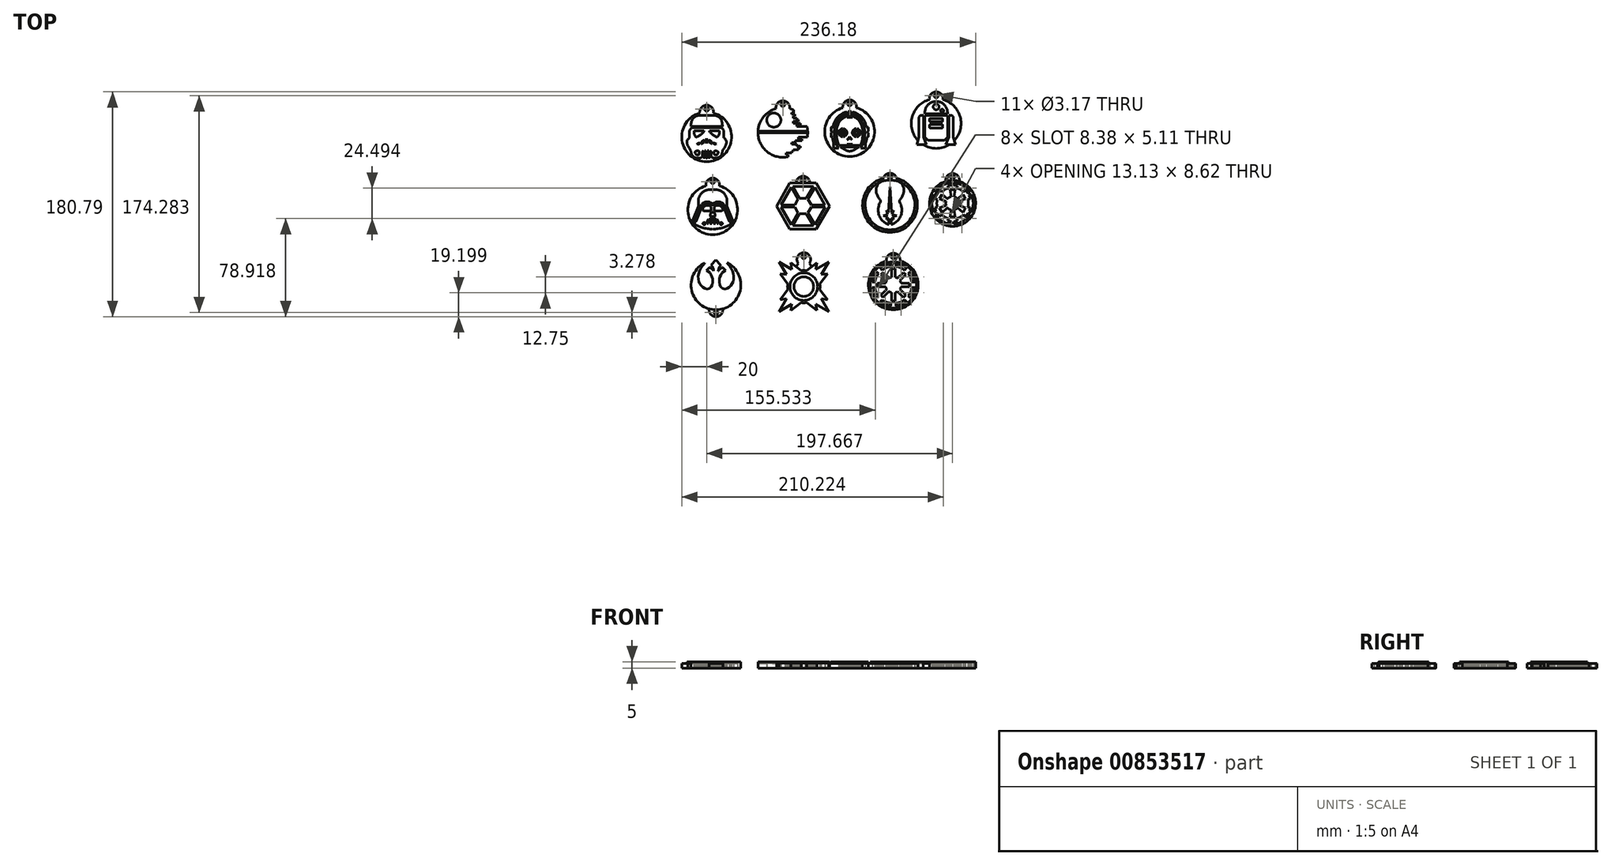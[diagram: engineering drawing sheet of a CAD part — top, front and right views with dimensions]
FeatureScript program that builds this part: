
annotation { "Feature Type Name" : "Feature", "Feature Type Description" : "" }
export const myFeature = defineFeature(function(context is Context, id is Id, definition is map)
    precondition{}
    {
        {
            var Q0;
            Q0=qCreatedBy(makeId("Top.planeOp"),FACE);
            var sketch = newSketch(context, id + "F0", { "sketchPlane" : qUnion([Q0])});
            skCircle(sketch, "E0", {"center": v(-100.44, 60.78) * mm, "radius": 20 * mm});
            skArc(sketch, "E1", {"start": v(-95, 80.02) * mm, "mid": v(-100.44, 86.28) * mm, "end": v(-105.89, 80.02) * mm});
            skCircle(sketch, "E2", {"center": v(-100.44, 83.03) * mm, "radius": 1.59 * mm});
            skLineSegment(sketch, "E3", {"start": v(-100.44, 78.18) * mm, "end": v(-105.77, 78.18) * mm});
            skFitSpline(sketch, "E4", {"points": [v(-105.77, 78.18) * mm, v(-108.26, 77.7) * mm, v(-111.1, 76.07) * mm, v(-112.23, 74.28) * mm, v(-112.98, 71.44) * mm, v(-113.03, 69.29) * mm], "startDerivative": vector(-12.14, -1.3) * mm, "endDerivative": vector(0.48, -11.2) * mm});
            skLineSegment(sketch, "E5", {"start": v(-113.03, 69.29) * mm, "end": v(-100.44, 69.29) * mm});
            skLineSegment(sketch, "E6", {"start": v(-100.44, 68.37) * mm, "end": v(-112.52, 68.37) * mm});
            skLineSegment(sketch, "E7", {"start": v(-112.52, 68.37) * mm, "end": v(-114.2, 66.04) * mm});
            skLineSegment(sketch, "E8", {"start": v(-114.2, 66.04) * mm, "end": v(-114.2, 60.06) * mm});
            skFitSpline(sketch, "E9", {"points": [v(-114.2, 60.06) * mm, v(-115.3, 59.1) * mm, v(-116.22, 57.54) * mm, v(-116.26, 55.78) * mm, v(-115.42, 53.27) * mm, v(-113.28, 49.95) * mm], "startDerivative": vector(-7.03, -5.26) * mm, "endDerivative": vector(9.04, -12.66) * mm});
            skFitSpline(sketch, "E10", {"points": [v(-113.28, 49.95) * mm, v(-113.02, 48.5) * mm, v(-112.3, 46.4) * mm, v(-111.03, 44.84) * mm, v(-109.24, 44) * mm, v(-107.26, 43.62) * mm, v(-105.24, 44.07) * mm, v(-103.86, 44.76) * mm], "startDerivative": vector(1.7, -10.88) * mm, "endDerivative": vector(9.96, 5.56) * mm});
            skLineSegment(sketch, "E11", {"start": v(-103.86, 44.76) * mm, "end": v(-103.86, 49.13) * mm});
            skLineSegment(sketch, "E12", {"start": v(-103.86, 49.13) * mm, "end": v(-103.07, 49.69) * mm});
            skLineSegment(sketch, "E13", {"start": v(-103.07, 49.69) * mm, "end": v(-103.07, 44.4) * mm});
            skFitSpline(sketch, "E14", {"points": [v(-103.07, 44.4) * mm, v(-102.64, 43.98) * mm, v(-102.12, 44.11) * mm, v(-101.98, 44.4) * mm], "startDerivative": vector(1, -1.45) * mm, "endDerivative": vector(0.3, 1.11) * mm});
            skLineSegment(sketch, "E15", {"start": v(-101.98, 44.4) * mm, "end": v(-101.98, 49.69) * mm});
            skLineSegment(sketch, "E16", {"start": v(-101.98, 49.69) * mm, "end": v(-101.2, 49.69) * mm});
            skLineSegment(sketch, "E17", {"start": v(-101.2, 49.69) * mm, "end": v(-101.2, 44.4) * mm});
            skFitSpline(sketch, "E18", {"points": [v(-101.2, 44.4) * mm, v(-100.97, 43.94) * mm, v(-100.61, 43.77) * mm, v(-100.44, 43.77) * mm], "startDerivative": vector(0.44, -1.3) * mm, "endDerivative": vector(0.66, 0.06) * mm});
            skLineSegment(sketch, "E19", {"start": v(-102.6, 65.55) * mm, "end": v(-110.61, 65.55) * mm});
            skLineSegment(sketch, "E20", {"start": v(-102.6, 65.55) * mm, "end": v(-102.6, 64.96) * mm});
            skFitSpline(sketch, "E21", {"points": [v(-110.61, 65.55) * mm, v(-110.61, 63.59) * mm, v(-110, 61.89) * mm, v(-108.94, 60.78) * mm, v(-107.62, 61) * mm, v(-105.2, 62.61) * mm, v(-102.6, 64.96) * mm], "startDerivative": vector(-0.88, -12.5) * mm, "endDerivative": vector(11.82, 11.31) * mm});
            skFitSpline(sketch, "E22", {"points": [v(-108.1, 55.17) * mm, v(-107.08, 55.66) * mm, v(-106, 55.74) * mm, v(-105.95, 55.5) * mm, v(-106.43, 55.06) * mm, v(-107.16, 54.9) * mm, v(-108.1, 55.17) * mm]});
            skLineSegment(sketch, "E23.bottom", {"start": v(-100.44, 58.8) * mm, "end": v(-99.36, 58.8) * mm});
            skLineSegment(sketch, "E23.top", {"start": v(-100.44, 56.6) * mm, "end": v(-99.36, 56.6) * mm});
            skLineSegment(sketch, "E23.left", {"start": v(-100.44, 58.8) * mm, "end": v(-100.44, 56.6) * mm});
            skLineSegment(sketch, "E23.right", {"start": v(-99.36, 58.8) * mm, "end": v(-99.36, 56.6) * mm});
            skLineSegment(sketch, "E24", {"start": v(-98.39, 58.2) * mm, "end": v(-98.39, 56.48) * mm});
            skLineSegment(sketch, "E25", {"start": v(-98.39, 56.48) * mm, "end": v(-96.69, 55.32) * mm});
            skLineSegment(sketch, "E26", {"start": v(-96.69, 55.32) * mm, "end": v(-96.1, 55.32) * mm});
            skLineSegment(sketch, "E27", {"start": v(-96.1, 55.32) * mm, "end": v(-96.1, 56.03) * mm});
            skFitSpline(sketch, "E28", {"points": [v(-98.39, 58.2) * mm, v(-97.3, 57.74) * mm, v(-96.51, 57) * mm, v(-96.1, 56.03) * mm], "startDerivative": vector(3.26, -1.14) * mm, "endDerivative": vector(0.98, -3.12) * mm});
            skFitSpline(sketch, "E29", {"points": [v(-108.72, 49.43) * mm, v(-109.59, 48.85) * mm, v(-109.81, 47.92) * mm, v(-109.01, 46.77) * mm, v(-107.66, 46.12) * mm, v(-106.64, 46.5) * mm, v(-106.32, 47.21) * mm, v(-106.29, 48.4) * mm, v(-106.54, 49.14) * mm, v(-107.34, 49.65) * mm, v(-108.72, 49.43) * mm]});
            skLineSegment(sketch, "E30.MirrorCS", {"start": v(-100.44, 78.18) * mm, "end": v(-95.11, 78.18) * mm});
            skFitSpline(sketch, "E31.MirrorCS", {"points": [v(-95.11, 78.18) * mm, v(-92.62, 77.7) * mm, v(-89.78, 76.07) * mm, v(-88.65, 74.28) * mm, v(-87.9, 71.44) * mm, v(-87.85, 69.29) * mm], "startDerivative": vector(12.14, -1.3) * mm, "endDerivative": vector(-0.48, -11.2) * mm});
            skLineSegment(sketch, "E32.MirrorCS", {"start": v(-87.85, 69.29) * mm, "end": v(-100.44, 69.29) * mm});
            skLineSegment(sketch, "E33.MirrorCS", {"start": v(-100.44, 68.37) * mm, "end": v(-88.36, 68.37) * mm});
            skLineSegment(sketch, "E34.MirrorCS", {"start": v(-88.36, 68.37) * mm, "end": v(-86.68, 66.04) * mm});
            skLineSegment(sketch, "E35.MirrorCS", {"start": v(-86.68, 66.04) * mm, "end": v(-86.68, 60.06) * mm});
            skLineSegment(sketch, "E36.MirrorCS", {"start": v(-98.28, 65.55) * mm, "end": v(-90.27, 65.55) * mm});
            skFitSpline(sketch, "E37.MirrorCS", {"points": [v(-90.27, 65.55) * mm, v(-90.27, 63.59) * mm, v(-90.89, 61.89) * mm, v(-91.94, 60.78) * mm, v(-93.26, 61) * mm, v(-95.69, 62.61) * mm, v(-98.28, 64.96) * mm], "startDerivative": vector(0.88, -12.5) * mm, "endDerivative": vector(-11.82, 11.31) * mm});
            skLineSegment(sketch, "E38.MirrorCS", {"start": v(-101.52, 58.8) * mm, "end": v(-101.52, 56.6) * mm});
            skLineSegment(sketch, "E39.MirrorCS", {"start": v(-100.44, 58.8) * mm, "end": v(-101.52, 58.8) * mm});
            skLineSegment(sketch, "E40.MirrorCS", {"start": v(-100.44, 56.6) * mm, "end": v(-101.52, 56.6) * mm});
            skFitSpline(sketch, "E41.MirrorC", {"points": [v(-92.78, 55.17) * mm, v(-93.8, 55.66) * mm, v(-94.88, 55.74) * mm, v(-94.93, 55.5) * mm, v(-94.45, 55.06) * mm, v(-93.72, 54.9) * mm, v(-92.78, 55.17) * mm]});
            skLineSegment(sketch, "E42.MirrorCS", {"start": v(-102.5, 56.48) * mm, "end": v(-104.2, 55.32) * mm});
            skLineSegment(sketch, "E43.MirrorCS", {"start": v(-102.5, 58.2) * mm, "end": v(-102.5, 56.48) * mm});
            skLineSegment(sketch, "E44.MirrorCS", {"start": v(-104.2, 55.32) * mm, "end": v(-104.77, 55.32) * mm});
            skLineSegment(sketch, "E45.MirrorCS", {"start": v(-104.77, 55.32) * mm, "end": v(-104.77, 56.03) * mm});
            skFitSpline(sketch, "E46.MirrorCS", {"points": [v(-102.5, 58.2) * mm, v(-103.57, 57.74) * mm, v(-104.37, 57) * mm, v(-104.77, 56.03) * mm], "startDerivative": vector(-3.26, -1.14) * mm, "endDerivative": vector(-0.98, -3.12) * mm});
            skFitSpline(sketch, "E47.MirrorCS", {"points": [v(-86.68, 60.06) * mm, v(-85.57, 59.1) * mm, v(-84.66, 57.54) * mm, v(-84.62, 55.78) * mm, v(-85.46, 53.27) * mm, v(-87.6, 49.95) * mm], "startDerivative": vector(7.03, -5.26) * mm, "endDerivative": vector(-9.04, -12.66) * mm});
            skFitSpline(sketch, "E48.MirrorCS", {"points": [v(-87.6, 49.95) * mm, v(-87.86, 48.5) * mm, v(-88.59, 46.4) * mm, v(-89.85, 44.84) * mm, v(-91.64, 44) * mm, v(-93.62, 43.62) * mm, v(-95.64, 44.07) * mm, v(-97.02, 44.76) * mm], "startDerivative": vector(-1.7, -10.88) * mm, "endDerivative": vector(-9.96, 5.56) * mm});
            skFitSpline(sketch, "E49.MirrorC", {"points": [v(-92.16, 49.43) * mm, v(-91.3, 48.85) * mm, v(-91.07, 47.92) * mm, v(-91.87, 46.77) * mm, v(-93.22, 46.12) * mm, v(-94.24, 46.5) * mm, v(-94.56, 47.21) * mm, v(-94.6, 48.4) * mm, v(-94.34, 49.14) * mm, v(-93.54, 49.65) * mm, v(-92.16, 49.43) * mm]});
            skLineSegment(sketch, "E50.MirrorCS", {"start": v(-97.02, 44.76) * mm, "end": v(-97.02, 49.13) * mm});
            skLineSegment(sketch, "E51.MirrorCS", {"start": v(-97.02, 49.13) * mm, "end": v(-97.8, 49.69) * mm});
            skLineSegment(sketch, "E52.MirrorCS", {"start": v(-97.8, 49.69) * mm, "end": v(-97.8, 44.4) * mm});
            skLineSegment(sketch, "E53.MirrorCS", {"start": v(-98.9, 44.4) * mm, "end": v(-98.9, 49.69) * mm});
            skLineSegment(sketch, "E54.MirrorCS", {"start": v(-98.9, 49.69) * mm, "end": v(-99.67, 49.69) * mm});
            skLineSegment(sketch, "E55.MirrorCS", {"start": v(-99.67, 49.69) * mm, "end": v(-99.67, 44.4) * mm});
            skFitSpline(sketch, "E56.MirrorCS", {"points": [v(-99.67, 44.4) * mm, v(-99.91, 43.94) * mm, v(-100.27, 43.77) * mm, v(-100.44, 43.77) * mm], "startDerivative": vector(-0.44, -1.3) * mm, "endDerivative": vector(-0.66, 0.06) * mm});
            skFitSpline(sketch, "E57.MirrorCS", {"points": [v(-97.8, 44.4) * mm, v(-98.24, 43.98) * mm, v(-98.76, 44.11) * mm, v(-98.9, 44.4) * mm], "startDerivative": vector(-1, -1.45) * mm, "endDerivative": vector(-0.3, 1.11) * mm});
            skLineSegment(sketch, "E58", {"start": v(-98.28, 65.55) * mm, "end": v(-98.28, 64.96) * mm});
            skSolve(sketch);
        }
        {
            var Q0;
            Q0=qCreatedBy(makeId("Top.planeOp"),FACE);
            var sketch = newSketch(context, id + "F1", { "sketchPlane" : qUnion([Q0])});
            skArc(sketch, "E59", {"start": v(-30.66, 82.44) * mm, "mid": v(-59.08, 66.65) * mm, "end": v(-35.01, 44.8) * mm});
            skArc(sketch, "E60", {"start": v(-33.76, 83.6) * mm, "mid": v(-39.21, 89.85) * mm, "end": v(-44.66, 83.6) * mm});
            skCircle(sketch, "E61", {"center": v(-39.21, 86.8) * mm, "radius": 1.59 * mm});
            skCircle(sketch, "E62", {"center": v(-46.46, 74.27) * mm, "radius": 5.66 * mm});
            skLineSegment(sketch, "E63", {"start": v(-30.66, 82.44) * mm, "end": v(-30.66, 80.15) * mm});
            skLineSegment(sketch, "E64", {"start": v(-30.66, 80.15) * mm, "end": v(-32.2, 80.15) * mm});
            skLineSegment(sketch, "E65", {"start": v(-32.2, 80.15) * mm, "end": v(-32.2, 78.86) * mm});
            skLineSegment(sketch, "E66", {"start": v(-32.2, 78.86) * mm, "end": v(-29.52, 78.86) * mm});
            skLineSegment(sketch, "E67", {"start": v(-29.52, 78.86) * mm, "end": v(-29.52, 77.4) * mm});
            skLineSegment(sketch, "E68", {"start": v(-29.52, 77.4) * mm, "end": v(-30.9, 77.4) * mm});
            skLineSegment(sketch, "E69", {"start": v(-30.9, 77.4) * mm, "end": v(-30.9, 75.98) * mm});
            skLineSegment(sketch, "E70", {"start": v(-30.9, 75.98) * mm, "end": v(-28.1, 75.98) * mm});
            skLineSegment(sketch, "E71", {"start": v(-28.1, 75.98) * mm, "end": v(-28.1, 74.48) * mm});
            skLineSegment(sketch, "E72", {"start": v(-28.1, 74.48) * mm, "end": v(-26.61, 74.48) * mm});
            skLineSegment(sketch, "E73", {"start": v(-26.61, 74.48) * mm, "end": v(-26.61, 73.15) * mm});
            skLineSegment(sketch, "E74", {"start": v(-26.61, 73.15) * mm, "end": v(-30.79, 73.15) * mm});
            skLineSegment(sketch, "E75", {"start": v(-30.79, 73.15) * mm, "end": v(-30.79, 71.78) * mm});
            skLineSegment(sketch, "E76", {"start": v(-30.79, 71.78) * mm, "end": v(-25.24, 71.78) * mm});
            skLineSegment(sketch, "E77", {"start": v(-25.24, 71.78) * mm, "end": v(-25.24, 70.29) * mm});
            skLineSegment(sketch, "E78", {"start": v(-25.24, 70.29) * mm, "end": v(-28, 70.29) * mm});
            skLineSegment(sketch, "E79", {"start": v(-28, 70.29) * mm, "end": v(-28, 69.08) * mm});
            skLineSegment(sketch, "E80", {"start": v(-28, 69.08) * mm, "end": v(-19.78, 69.08) * mm});
            skLineSegment(sketch, "E81", {"start": v(-59.18, 65.46) * mm, "end": v(-19.24, 65.46) * mm});
            skLineSegment(sketch, "E82", {"start": v(-59.2, 64.02) * mm, "end": v(-19.21, 64.02) * mm});
            skLineSegment(sketch, "E83", {"start": v(-19.59, 60.49) * mm, "end": v(-26.58, 60.49) * mm});
            skLineSegment(sketch, "E84", {"start": v(-26.58, 60.49) * mm, "end": v(-26.58, 59.12) * mm});
            skLineSegment(sketch, "E85", {"start": v(-26.58, 59.12) * mm, "end": v(-23.87, 59.12) * mm});
            skLineSegment(sketch, "E86", {"start": v(-23.87, 59.12) * mm, "end": v(-23.87, 57.67) * mm});
            skLineSegment(sketch, "E87", {"start": v(-23.87, 57.67) * mm, "end": v(-29.3, 57.67) * mm});
            skLineSegment(sketch, "E88", {"start": v(-29.3, 57.67) * mm, "end": v(-29.3, 56.14) * mm});
            skLineSegment(sketch, "E89", {"start": v(-29.3, 56.14) * mm, "end": v(-32.23, 56.14) * mm});
            skLineSegment(sketch, "E90", {"start": v(-32.23, 56.14) * mm, "end": v(-32.23, 54.92) * mm});
            skLineSegment(sketch, "E91", {"start": v(-32.23, 54.92) * mm, "end": v(-28.03, 54.92) * mm});
            skLineSegment(sketch, "E92", {"start": v(-28.03, 54.92) * mm, "end": v(-28.03, 53.4) * mm});
            skLineSegment(sketch, "E93", {"start": v(-28.03, 53.4) * mm, "end": v(-25.29, 53.4) * mm});
            skLineSegment(sketch, "E94", {"start": v(-25.29, 53.4) * mm, "end": v(-25.29, 51.9) * mm});
            skLineSegment(sketch, "E95", {"start": v(-25.29, 51.9) * mm, "end": v(-26.58, 51.9) * mm});
            skLineSegment(sketch, "E96", {"start": v(-26.58, 51.9) * mm, "end": v(-26.58, 50.46) * mm});
            skLineSegment(sketch, "E97", {"start": v(-26.58, 50.46) * mm, "end": v(-30.82, 50.46) * mm});
            skLineSegment(sketch, "E98", {"start": v(-30.82, 50.46) * mm, "end": v(-30.82, 49.28) * mm});
            skLineSegment(sketch, "E99", {"start": v(-30.82, 49.28) * mm, "end": v(-32.23, 49.28) * mm});
            skLineSegment(sketch, "E100", {"start": v(-32.23, 49.28) * mm, "end": v(-32.23, 47.79) * mm});
            skLineSegment(sketch, "E101", {"start": v(-32.23, 47.79) * mm, "end": v(-36.5, 47.79) * mm});
            skLineSegment(sketch, "E102", {"start": v(-36.5, 47.79) * mm, "end": v(-36.5, 46.45) * mm});
            skLineSegment(sketch, "E103", {"start": v(-36.5, 46.45) * mm, "end": v(-35.01, 46.45) * mm});
            skLineSegment(sketch, "E104", {"start": v(-35.01, 46.45) * mm, "end": v(-35.01, 44.8) * mm});
            skArc(sketch, "E105.trimOffspring", {"start": v(-19.59, 60.49) * mm, "mid": v(-19.22, 64.8) * mm, "end": v(-19.78, 69.08) * mm});
            skSolve(sketch);
        }
        {
            var Q0;
            Q0=qCreatedBy(makeId("Top.planeOp"),FACE);
            var sketch = newSketch(context, id + "F2", { "sketchPlane" : qUnion([Q0])});
            skCircle(sketch, "E106", {"center": v(14.5, 65.01) * mm, "radius": 20 * mm});
            skArc(sketch, "E107", {"start": v(19.94, 84.25) * mm, "mid": v(14.5, 90.51) * mm, "end": v(9.05, 84.25) * mm});
            skCircle(sketch, "E108", {"center": v(14.5, 87.35) * mm, "radius": 1.59 * mm});
            skLineSegment(sketch, "E109.bottom", {"start": v(14.5, 81.26) * mm, "end": v(13.26, 81.26) * mm});
            skLineSegment(sketch, "E109.top", {"start": v(14.5, 77.67) * mm, "end": v(13.26, 77.67) * mm});
            skLineSegment(sketch, "E109.right", {"start": v(13.26, 81.26) * mm, "end": v(13.26, 77.67) * mm});
            skPoint(sketch, "E110.1.internal.snap0", {"position": v(13.26, 79.46) * mm});
            skFitSpline(sketch, "E110", {"points": [v(12.26, 80.95) * mm, v(8.57, 79.46) * mm, v(4.65, 76.5) * mm, v(2.7, 73.58) * mm, v(1.48, 70.56) * mm, v(1.13, 68.67) * mm], "startDerivative": vector(-16.9, -5.64) * mm, "endDerivative": vector(-1.55, -11.93) * mm});
            skLineSegment(sketch, "E111", {"start": v(12.26, 80.95) * mm, "end": v(12.26, 79.13) * mm});
            skFitSpline(sketch, "E112", {"points": [v(12.26, 79.13) * mm, v(9.79, 78.1) * mm, v(7, 76.24) * mm, v(4.65, 73.45) * mm, v(3.53, 70.85) * mm, v(2.44, 66.94) * mm, v(2.28, 60.97) * mm, v(2.83, 58.02) * mm, v(3.76, 54.81) * mm, v(5.65, 51.7) * mm], "startDerivative": vector(-25.43, -9.49) * mm, "endDerivative": vector(18.91, -26.8) * mm});
            skLineSegment(sketch, "E113", {"start": v(5.65, 51.7) * mm, "end": v(1.66, 51.7) * mm});
            skLineSegment(sketch, "E114", {"start": v(1.66, 51.7) * mm, "end": v(1.66, 55.86) * mm});
            skFitSpline(sketch, "E115", {"points": [v(1.66, 55.86) * mm, v(1.2, 57.2) * mm, v(0.74, 59.74) * mm, v(0.77, 60.69) * mm], "startDerivative": vector(-1.45, 3.7) * mm, "endDerivative": vector(0.33, 3.09) * mm});
            skLineSegment(sketch, "E116", {"start": v(0.56, 65.2) * mm, "end": v(0.56, 64.2) * mm});
            skLineSegment(sketch, "E117", {"start": v(0.56, 64.2) * mm, "end": v(-0.1, 64.2) * mm});
            skLineSegment(sketch, "E118", {"start": v(0.77, 60.69) * mm, "end": v(-0.1, 60.69) * mm});
            skLineSegment(sketch, "E119", {"start": v(-0.47, 61.06) * mm, "end": v(-0.47, 63.83) * mm});
            skLineSegment(sketch, "E120", {"start": v(0.56, 65.2) * mm, "end": v(-0.1, 65.2) * mm});
            skLineSegment(sketch, "E121", {"start": v(-0.47, 65.56) * mm, "end": v(-0.47, 68.3) * mm});
            skLineSegment(sketch, "E122", {"start": v(-0.1, 68.67) * mm, "end": v(1.13, 68.67) * mm});
            skPoint(sketch, "E123.visualSharp", {"position": v(-0.47, 68.67) * mm});
            skArc(sketch, "E123.filletArc", {"start": v(-0.1, 68.67) * mm, "mid": v(-0.36, 68.56) * mm, "end": v(-0.47, 68.3) * mm});
            skPoint(sketch, "E124.visualSharp", {"position": v(-0.47, 65.2) * mm});
            skArc(sketch, "E124.filletArc", {"start": v(-0.47, 65.56) * mm, "mid": v(-0.36, 65.3) * mm, "end": v(-0.1, 65.2) * mm});
            skPoint(sketch, "E125.visualSharp", {"position": v(-0.47, 64.2) * mm});
            skArc(sketch, "E125.filletArc", {"start": v(-0.1, 64.2) * mm, "mid": v(-0.36, 64.09) * mm, "end": v(-0.47, 63.83) * mm});
            skPoint(sketch, "E126.visualSharp", {"position": v(-0.47, 60.69) * mm});
            skArc(sketch, "E126.filletArc", {"start": v(-0.47, 61.06) * mm, "mid": v(-0.36, 60.8) * mm, "end": v(-0.1, 60.69) * mm});
            skArc(sketch, "E127", {"start": v(6.65, 66.42) * mm, "mid": v(5.74, 64.13) * mm, "end": v(6.65, 61.84) * mm});
            skLineSegment(sketch, "E128", {"start": v(6.65, 66.42) * mm, "end": v(6.65, 61.84) * mm});
            skLineSegment(sketch, "E129", {"start": v(7.23, 66.9) * mm, "end": v(7.23, 61.36) * mm});
            skArc(sketch, "E130", {"start": v(8.7, 65.25) * mm, "mid": v(7.88, 64.13) * mm, "end": v(8.7, 63) * mm});
            skLineSegment(sketch, "E131", {"start": v(8.7, 67.44) * mm, "end": v(8.7, 65.25) * mm});
            skLineSegment(sketch, "E132.trimOffspring", {"start": v(8.7, 63) * mm, "end": v(8.7, 60.83) * mm});
            skLineSegment(sketch, "E133.MirrorCS", {"start": v(9.42, 67.44) * mm, "end": v(9.42, 65.25) * mm});
            skLineSegment(sketch, "E134.MirrorCS", {"start": v(9.42, 63) * mm, "end": v(9.42, 60.83) * mm});
            skLineSegment(sketch, "E135.MirrorCS", {"start": v(10.89, 66.9) * mm, "end": v(10.89, 61.36) * mm});
            skLineSegment(sketch, "E136.MirrorCS", {"start": v(11.46, 66.42) * mm, "end": v(11.46, 61.84) * mm});
            skArc(sketch, "E137.trimOffspring", {"start": v(9.42, 63) * mm, "mid": v(10.24, 64.13) * mm, "end": v(9.42, 65.25) * mm});
            skArc(sketch, "E138.trimOffspring", {"start": v(7.23, 61.36) * mm, "mid": v(7.93, 61) * mm, "end": v(8.7, 60.83) * mm});
            skArc(sketch, "E139.trimOffspring", {"start": v(11.46, 61.84) * mm, "mid": v(12.38, 64.13) * mm, "end": v(11.46, 66.42) * mm});
            skArc(sketch, "E140.trimOffspring", {"start": v(9.42, 60.83) * mm, "mid": v(10.18, 61) * mm, "end": v(10.89, 61.36) * mm});
            skArc(sketch, "E141.trimOffspring", {"start": v(8.7, 67.44) * mm, "mid": v(7.93, 67.26) * mm, "end": v(7.23, 66.9) * mm});
            skArc(sketch, "E142.trimOffspring", {"start": v(10.89, 66.9) * mm, "mid": v(10.18, 67.26) * mm, "end": v(9.42, 67.44) * mm});
            skFitSpline(sketch, "E143", {"points": [v(12.23, 77.45) * mm, v(9.7, 76.26) * mm, v(7.08, 74.03) * mm, v(5.1, 70.52) * mm, v(3.97, 66.28) * mm, v(3.9, 62.67) * mm, v(4.4, 58.22) * mm, v(5.38, 55.17) * mm, v(6.05, 53.9) * mm], "startDerivative": vector(-22.24, -8.97) * mm, "endDerivative": vector(8.1, -13.8) * mm});
            skLineSegment(sketch, "E144", {"start": v(6.05, 53.9) * mm, "end": v(12.23, 53.9) * mm});
            skLineSegment(sketch, "E145", {"start": v(12.23, 53.9) * mm, "end": v(12.23, 54.98) * mm});
            skLineSegment(sketch, "E146", {"start": v(12.23, 54.98) * mm, "end": v(14.5, 54.98) * mm});
            skLineSegment(sketch, "E147", {"start": v(12.23, 77.45) * mm, "end": v(12.23, 76.62) * mm});
            skLineSegment(sketch, "E148", {"start": v(12.23, 76.62) * mm, "end": v(14.5, 76.62) * mm});
            skLineSegment(sketch, "E149", {"start": v(14.5, 60.76) * mm, "end": v(12.42, 58.48) * mm});
            skLineSegment(sketch, "E150", {"start": v(12.42, 58.48) * mm, "end": v(14.5, 59.5) * mm});
            skLineSegment(sketch, "E151", {"start": v(14.5, 52.76) * mm, "end": v(6.84, 52.76) * mm});
            skFitSpline(sketch, "E152", {"points": [v(6.84, 52.76) * mm, v(9.97, 50.85) * mm, v(12.97, 49.5) * mm, v(14.5, 49.26) * mm], "startDerivative": vector(7.92, -5.08) * mm, "endDerivative": vector(5.64, -0.43) * mm});
            skLineSegment(sketch, "E153.MirrorCS", {"start": v(14.5, 52.76) * mm, "end": v(22.15, 52.76) * mm});
            skFitSpline(sketch, "E154.MirrorCS", {"points": [v(22.15, 52.76) * mm, v(19.02, 50.85) * mm, v(16.02, 49.5) * mm, v(14.5, 49.26) * mm], "startDerivative": vector(-7.92, -5.08) * mm, "endDerivative": vector(-5.64, -0.43) * mm});
            skLineSegment(sketch, "E155.MirrorCS", {"start": v(22.94, 53.9) * mm, "end": v(16.76, 53.9) * mm});
            skLineSegment(sketch, "E156.MirrorCS", {"start": v(16.76, 53.9) * mm, "end": v(16.76, 54.98) * mm});
            skLineSegment(sketch, "E157.MirrorCS", {"start": v(16.76, 54.98) * mm, "end": v(14.5, 54.98) * mm});
            skFitSpline(sketch, "E158.MirrorCS", {"points": [v(16.76, 77.45) * mm, v(19.3, 76.26) * mm, v(21.91, 74.03) * mm, v(23.88, 70.52) * mm, v(25.01, 66.28) * mm, v(25.1, 62.67) * mm, v(24.58, 58.22) * mm, v(23.61, 55.17) * mm, v(22.94, 53.9) * mm], "startDerivative": vector(22.24, -8.97) * mm, "endDerivative": vector(-8.1, -13.8) * mm});
            skFitSpline(sketch, "E159.MirrorCS", {"points": [v(16.73, 79.13) * mm, v(19.2, 78.1) * mm, v(22, 76.24) * mm, v(24.33, 73.45) * mm, v(25.45, 70.85) * mm, v(26.55, 66.94) * mm, v(26.7, 60.97) * mm, v(26.16, 58.02) * mm, v(25.23, 54.81) * mm, v(23.34, 51.7) * mm], "startDerivative": vector(25.43, -9.49) * mm, "endDerivative": vector(-18.91, -26.8) * mm});
            skLineSegment(sketch, "E160.MirrorCS", {"start": v(27.33, 51.7) * mm, "end": v(27.33, 55.86) * mm});
            skFitSpline(sketch, "E161.MirrorCS", {"points": [v(27.33, 55.86) * mm, v(27.78, 57.2) * mm, v(28.24, 59.74) * mm, v(28.22, 60.69) * mm], "startDerivative": vector(1.45, 3.7) * mm, "endDerivative": vector(-0.33, 3.09) * mm});
            skLineSegment(sketch, "E162.MirrorCS", {"start": v(28.22, 60.69) * mm, "end": v(29.09, 60.69) * mm});
            skArc(sketch, "E163.MirrorCS", {"start": v(29.46, 61.06) * mm, "mid": v(29.35, 60.8) * mm, "end": v(29.09, 60.69) * mm});
            skLineSegment(sketch, "E164.MirrorCS", {"start": v(29.46, 61.06) * mm, "end": v(29.46, 63.83) * mm});
            skArc(sketch, "E165.MirrorCS", {"start": v(29.09, 64.2) * mm, "mid": v(29.35, 64.09) * mm, "end": v(29.46, 63.83) * mm});
            skLineSegment(sketch, "E166.MirrorCS", {"start": v(28.43, 64.2) * mm, "end": v(29.09, 64.2) * mm});
            skLineSegment(sketch, "E167.MirrorCS", {"start": v(28.43, 65.2) * mm, "end": v(28.43, 64.2) * mm});
            skLineSegment(sketch, "E168.MirrorCS", {"start": v(28.43, 65.2) * mm, "end": v(29.09, 65.2) * mm});
            skArc(sketch, "E169.MirrorCS", {"start": v(29.46, 65.56) * mm, "mid": v(29.35, 65.3) * mm, "end": v(29.09, 65.2) * mm});
            skLineSegment(sketch, "E170.MirrorCS", {"start": v(29.46, 65.56) * mm, "end": v(29.46, 68.3) * mm});
            skArc(sketch, "E171.MirrorCS", {"start": v(29.09, 68.67) * mm, "mid": v(29.35, 68.56) * mm, "end": v(29.46, 68.3) * mm});
            skLineSegment(sketch, "E172.MirrorCS", {"start": v(29.09, 68.67) * mm, "end": v(27.86, 68.67) * mm});
            skFitSpline(sketch, "E173.MirrorCS", {"points": [v(16.73, 80.95) * mm, v(20.42, 79.46) * mm, v(24.33, 76.5) * mm, v(26.29, 73.58) * mm, v(27.5, 70.56) * mm, v(27.86, 68.67) * mm], "startDerivative": vector(16.9, -5.64) * mm, "endDerivative": vector(1.55, -11.93) * mm});
            skLineSegment(sketch, "E174.MirrorCS", {"start": v(14.5, 60.76) * mm, "end": v(16.57, 58.48) * mm});
            skLineSegment(sketch, "E175.MirrorCS", {"start": v(16.57, 58.48) * mm, "end": v(14.5, 59.5) * mm});
            skArc(sketch, "E176.MirrorCS", {"start": v(17.52, 61.84) * mm, "mid": v(16.6, 64.13) * mm, "end": v(17.52, 66.42) * mm});
            skLineSegment(sketch, "E177.MirrorCS", {"start": v(17.52, 66.42) * mm, "end": v(17.52, 61.84) * mm});
            skLineSegment(sketch, "E178.MirrorCS", {"start": v(18.1, 66.9) * mm, "end": v(18.1, 61.36) * mm});
            skArc(sketch, "E179.MirrorCS", {"start": v(19.57, 63) * mm, "mid": v(18.75, 64.13) * mm, "end": v(19.57, 65.25) * mm});
            skLineSegment(sketch, "E180.MirrorCS", {"start": v(19.57, 67.44) * mm, "end": v(19.57, 65.25) * mm});
            skLineSegment(sketch, "E181.MirrorCS", {"start": v(19.57, 63) * mm, "end": v(19.57, 60.83) * mm});
            skLineSegment(sketch, "E182.MirrorCS", {"start": v(20.29, 63) * mm, "end": v(20.29, 60.83) * mm});
            skArc(sketch, "E183.MirrorCS", {"start": v(20.29, 65.25) * mm, "mid": v(21.1, 64.13) * mm, "end": v(20.29, 63) * mm});
            skLineSegment(sketch, "E184.MirrorCS", {"start": v(20.29, 67.44) * mm, "end": v(20.29, 65.25) * mm});
            skLineSegment(sketch, "E185.MirrorCS", {"start": v(21.76, 66.9) * mm, "end": v(21.76, 61.36) * mm});
            skLineSegment(sketch, "E186.MirrorCS", {"start": v(22.33, 66.42) * mm, "end": v(22.33, 61.84) * mm});
            skArc(sketch, "E187.MirrorCS", {"start": v(22.33, 66.42) * mm, "mid": v(23.25, 64.13) * mm, "end": v(22.33, 61.84) * mm});
            skArc(sketch, "E188.MirrorCS", {"start": v(21.76, 61.36) * mm, "mid": v(21.05, 61) * mm, "end": v(20.29, 60.83) * mm});
            skArc(sketch, "E189.MirrorCS", {"start": v(19.57, 60.83) * mm, "mid": v(18.8, 61) * mm, "end": v(18.1, 61.36) * mm});
            skArc(sketch, "E190.MirrorCS", {"start": v(20.29, 67.44) * mm, "mid": v(21.05, 67.26) * mm, "end": v(21.76, 66.9) * mm});
            skArc(sketch, "E191.MirrorCS", {"start": v(18.1, 66.9) * mm, "mid": v(18.8, 67.26) * mm, "end": v(19.57, 67.44) * mm});
            skLineSegment(sketch, "E192.MirrorCS", {"start": v(15.73, 81.26) * mm, "end": v(15.73, 77.67) * mm});
            skLineSegment(sketch, "E193.MirrorCS", {"start": v(16.76, 76.62) * mm, "end": v(14.5, 76.62) * mm});
            skLineSegment(sketch, "E194.MirrorCS", {"start": v(16.76, 77.45) * mm, "end": v(16.76, 76.62) * mm});
            skLineSegment(sketch, "E195.MirrorCS", {"start": v(14.5, 81.26) * mm, "end": v(15.73, 81.26) * mm});
            skLineSegment(sketch, "E196.MirrorCS", {"start": v(14.5, 77.67) * mm, "end": v(15.73, 77.67) * mm});
            skLineSegment(sketch, "E197.MirrorCS", {"start": v(23.34, 51.7) * mm, "end": v(27.33, 51.7) * mm});
            skLineSegment(sketch, "E198.MirrorCS", {"start": v(16.73, 80.95) * mm, "end": v(16.73, 79.13) * mm});
            skSolve(sketch);
        }
        {
            var Q0;
            Q0=qCreatedBy(makeId("Top.planeOp"),FACE);
            var sketch = newSketch(context, id + "F3", { "sketchPlane" : qUnion([Q0])});
            skArc(sketch, "E199", {"start": v(73.59, 54.46) * mm, "mid": v(84.04, 51.51) * mm, "end": v(94.5, 54.46) * mm});
            skArc(sketch, "E200", {"start": v(89.5, 90.75) * mm, "mid": v(84.04, 97.01) * mm, "end": v(78.6, 90.75) * mm});
            skCircle(sketch, "E201", {"center": v(84.04, 93.78) * mm, "radius": 1.59 * mm});
            skFitSpline(sketch, "E202", {"points": [v(84.04, 89.35) * mm, v(81.88, 89.08) * mm, v(79.11, 87.94) * mm, v(77.12, 86.17) * mm, v(75.75, 84) * mm, v(75.03, 81.6) * mm, v(74.94, 79.28) * mm], "startDerivative": vector(-13.48, -0.88) * mm, "endDerivative": vector(0.22, -14.46) * mm});
            skLineSegment(sketch, "E203", {"start": v(74.94, 79.28) * mm, "end": v(84.04, 79.28) * mm});
            skCircle(sketch, "E204", {"center": v(84.04, 84.95) * mm, "radius": 2.37 * mm});
            skCircle(sketch, "E205", {"center": v(88.86, 81.82) * mm, "radius": 1.22 * mm});
            skLineSegment(sketch, "E206", {"start": v(84.04, 78) * mm, "end": v(74.94, 78) * mm});
            skLineSegment(sketch, "E207", {"start": v(74.94, 78) * mm, "end": v(74.94, 60.59) * mm});
            skLineSegment(sketch, "E208", {"start": v(74.94, 60.59) * mm, "end": v(77.43, 58) * mm});
            skLineSegment(sketch, "E209", {"start": v(77.43, 58) * mm, "end": v(84.04, 58) * mm});
            skLineSegment(sketch, "E210.bottom", {"start": v(84.04, 75.6) * mm, "end": v(79.2, 75.6) * mm});
            skLineSegment(sketch, "E210.top", {"start": v(84.04, 72.97) * mm, "end": v(79.2, 72.97) * mm});
            skLineSegment(sketch, "E210.right", {"start": v(78.84, 75.23) * mm, "end": v(78.84, 73.34) * mm});
            skLineSegment(sketch, "E211.bottom", {"start": v(84.04, 70.66) * mm, "end": v(79.2, 70.66) * mm});
            skLineSegment(sketch, "E211.top", {"start": v(84.04, 67.94) * mm, "end": v(79.2, 67.94) * mm});
            skLineSegment(sketch, "E211.right", {"start": v(78.84, 70.29) * mm, "end": v(78.84, 68.3) * mm});
            skPoint(sketch, "E212.visualSharp", {"position": v(78.84, 75.6) * mm});
            skArc(sketch, "E212.filletArc", {"start": v(79.2, 75.6) * mm, "mid": v(78.95, 75.5) * mm, "end": v(78.84, 75.23) * mm});
            skPoint(sketch, "E213.visualSharp", {"position": v(78.84, 72.97) * mm});
            skArc(sketch, "E213.filletArc", {"start": v(78.84, 73.34) * mm, "mid": v(78.95, 73.08) * mm, "end": v(79.2, 72.97) * mm});
            skPoint(sketch, "E214.visualSharp", {"position": v(78.84, 70.66) * mm});
            skArc(sketch, "E214.filletArc", {"start": v(79.2, 70.66) * mm, "mid": v(78.95, 70.55) * mm, "end": v(78.84, 70.29) * mm});
            skPoint(sketch, "E215.visualSharp", {"position": v(78.84, 67.94) * mm});
            skArc(sketch, "E215.filletArc", {"start": v(78.84, 68.3) * mm, "mid": v(78.95, 68.04) * mm, "end": v(79.2, 67.94) * mm});
            skLineSegment(sketch, "E216", {"start": v(73.81, 78) * mm, "end": v(73.81, 60.5) * mm});
            skLineSegment(sketch, "E217", {"start": v(73.81, 60.5) * mm, "end": v(76.26, 54.46) * mm});
            skLineSegment(sketch, "E218", {"start": v(76.26, 54.46) * mm, "end": v(68.55, 54.46) * mm});
            skLineSegment(sketch, "E219", {"start": v(68.55, 54.46) * mm, "end": v(70.23, 60.5) * mm});
            skLineSegment(sketch, "E220", {"start": v(70.23, 60.5) * mm, "end": v(70.23, 75.87) * mm});
            skFitSpline(sketch, "E221", {"points": [v(70.23, 75.87) * mm, v(70.23, 76.39) * mm, v(70.56, 77.18) * mm, v(71.26, 77.91) * mm, v(73.81, 78.13) * mm], "startDerivative": vector(-0.32, 2.9) * mm, "endDerivative": vector(7.93, -0.18) * mm});
            skLineSegment(sketch, "E222", {"start": v(73.81, 78) * mm, "end": v(73.81, 78.13) * mm});
            skFitSpline(sketch, "E223.MirrorCS", {"points": [v(84.04, 89.35) * mm, v(86.21, 89.08) * mm, v(88.98, 87.94) * mm, v(90.97, 86.17) * mm, v(92.33, 84) * mm, v(93.06, 81.6) * mm, v(93.15, 79.28) * mm], "startDerivative": vector(13.48, -0.88) * mm, "endDerivative": vector(-0.22, -14.46) * mm});
            skLineSegment(sketch, "E224.MirrorCS", {"start": v(93.15, 79.28) * mm, "end": v(84.04, 79.28) * mm});
            skLineSegment(sketch, "E225.MirrorCS", {"start": v(84.04, 78) * mm, "end": v(93.15, 78) * mm});
            skLineSegment(sketch, "E226.MirrorCS", {"start": v(93.15, 78) * mm, "end": v(93.15, 60.59) * mm});
            skLineSegment(sketch, "E227.MirrorCS", {"start": v(93.15, 60.59) * mm, "end": v(90.66, 58) * mm});
            skLineSegment(sketch, "E228.MirrorCS", {"start": v(90.66, 58) * mm, "end": v(84.04, 58) * mm});
            skLineSegment(sketch, "E229.MirrorCS", {"start": v(84.04, 67.94) * mm, "end": v(88.88, 67.94) * mm});
            skArc(sketch, "E230.MirrorCS", {"start": v(89.25, 68.3) * mm, "mid": v(89.14, 68.04) * mm, "end": v(88.88, 67.94) * mm});
            skLineSegment(sketch, "E231.MirrorCS", {"start": v(89.25, 70.29) * mm, "end": v(89.25, 68.3) * mm});
            skArc(sketch, "E232.MirrorCS", {"start": v(88.88, 70.66) * mm, "mid": v(89.14, 70.55) * mm, "end": v(89.25, 70.29) * mm});
            skLineSegment(sketch, "E233.MirrorCS", {"start": v(84.04, 70.66) * mm, "end": v(88.88, 70.66) * mm});
            skLineSegment(sketch, "E234.MirrorCS", {"start": v(84.04, 72.97) * mm, "end": v(88.88, 72.97) * mm});
            skArc(sketch, "E235.MirrorCS", {"start": v(89.25, 73.34) * mm, "mid": v(89.14, 73.08) * mm, "end": v(88.88, 72.97) * mm});
            skLineSegment(sketch, "E236.MirrorCS", {"start": v(89.25, 75.23) * mm, "end": v(89.25, 73.34) * mm});
            skArc(sketch, "E237.MirrorCS", {"start": v(88.88, 75.6) * mm, "mid": v(89.14, 75.5) * mm, "end": v(89.25, 75.23) * mm});
            skLineSegment(sketch, "E238.MirrorCS", {"start": v(84.04, 75.6) * mm, "end": v(88.88, 75.6) * mm});
            skLineSegment(sketch, "E239.MirrorCS", {"start": v(94.28, 78) * mm, "end": v(94.28, 60.5) * mm});
            skLineSegment(sketch, "E240.MirrorCS", {"start": v(97.86, 60.5) * mm, "end": v(97.86, 75.87) * mm});
            skFitSpline(sketch, "E241.MirrorCS", {"points": [v(97.86, 75.87) * mm, v(97.86, 76.39) * mm, v(97.53, 77.18) * mm, v(96.83, 77.91) * mm, v(94.28, 78.13) * mm], "startDerivative": vector(0.32, 2.9) * mm, "endDerivative": vector(-7.93, -0.18) * mm});
            skLineSegment(sketch, "E242.MirrorCS", {"start": v(94.28, 78) * mm, "end": v(94.28, 78.13) * mm});
            skLineSegment(sketch, "E243.MirrorCS", {"start": v(99.54, 54.46) * mm, "end": v(97.86, 60.5) * mm});
            skLineSegment(sketch, "E244.MirrorCS", {"start": v(91.83, 54.46) * mm, "end": v(99.54, 54.46) * mm});
            skLineSegment(sketch, "E245.MirrorCS", {"start": v(94.28, 60.5) * mm, "end": v(91.83, 54.46) * mm});
            skArc(sketch, "E246.trimOffspring", {"start": v(98.61, 57.8) * mm, "mid": v(84.04, 91.51) * mm, "end": v(69.48, 57.8) * mm});
            skSolve(sketch);
        }
        {
            var Q0;
            Q0=qCreatedBy(makeId("Top.planeOp"),FACE);
            var sketch = newSketch(context, id + "F4", { "sketchPlane" : qUnion([Q0])});
            skArc(sketch, "E247", {"start": v(-101.05, 21.39) * mm, "mid": v(-95.6, -17.86) * mm, "end": v(-90.15, 21.39) * mm});
            skArc(sketch, "E248", {"start": v(-90.15, 21.39) * mm, "mid": v(-95.6, 27.64) * mm, "end": v(-101.05, 21.39) * mm});
            skCircle(sketch, "E249", {"center": v(-95.6, 24.88) * mm, "radius": 1.59 * mm});
            skLineSegment(sketch, "E250", {"start": v(-95.6, 18.35) * mm, "end": v(-98.77, 18.35) * mm});
            skFitSpline(sketch, "E251", {"points": [v(-98.77, 18.35) * mm, v(-102, 17.41) * mm, v(-104.91, 15.23) * mm, v(-106.83, 11.85) * mm, v(-107.15, 10.34) * mm], "startDerivative": vector(-12.5, -2.75) * mm, "endDerivative": vector(-0.88, -7.56) * mm});
            skLineSegment(sketch, "E252", {"start": v(-107.15, 10.34) * mm, "end": v(-107.15, 5.14) * mm});
            skLineSegment(sketch, "E253", {"start": v(-107.15, 5.14) * mm, "end": v(-111.67, -6.62) * mm});
            skFitSpline(sketch, "E254", {"points": [v(-111.67, -6.62) * mm, v(-111, -8.13) * mm, v(-108.03, -10.52) * mm, v(-103.82, -12.19) * mm, v(-97.26, -13.43) * mm, v(-95.6, -13.54) * mm], "startDerivative": vector(3, -10.53) * mm, "endDerivative": vector(9.52, -0.14) * mm});
            skArc(sketch, "E255", {"start": v(-109.91, -6.58) * mm, "mid": v(-109.54, -7.25) * mm, "end": v(-108.83, -6.95) * mm});
            skLineSegment(sketch, "E256", {"start": v(-109.91, -6.58) * mm, "end": v(-105.58, 4.37) * mm});
            skLineSegment(sketch, "E257", {"start": v(-108.83, -6.95) * mm, "end": v(-104.1, 4.9) * mm});
            skFitSpline(sketch, "E258", {"points": [v(-105.58, 4.37) * mm, v(-104.22, 6.79) * mm, v(-101.87, 8.36) * mm, v(-99.7, 8.61) * mm, v(-98.1, 8.3) * mm, v(-96.95, 7.74) * mm, v(-95.6, 7.06) * mm], "startDerivative": vector(5.68, 13) * mm, "endDerivative": vector(9.61, -4.7) * mm});
            skFitSpline(sketch, "E259", {"points": [v(-104.1, 4.9) * mm, v(-102.77, 6.72) * mm, v(-100.08, 7.62) * mm, v(-97.82, 7.03) * mm, v(-96.43, 6.3) * mm], "startDerivative": vector(4.2, 7.92) * mm, "endDerivative": vector(6.2, -3.55) * mm});
            skFitSpline(sketch, "E260", {"points": [v(-96.43, 6.3) * mm, v(-96.05, 6.06) * mm, v(-95.6, 6.02) * mm], "startDerivative": vector(0.72, -0.55) * mm, "endDerivative": vector(0.93, 0.02) * mm});
            skFitSpline(sketch, "E261", {"points": [v(-102.89, 1.3) * mm, v(-103.63, 2.04) * mm, v(-103.35, 3.7) * mm, v(-101.9, 5.22) * mm, v(-99.92, 5.78) * mm, v(-98.18, 5.5) * mm, v(-97, 4.37) * mm], "startDerivative": vector(-7.07, 4.58) * mm, "endDerivative": vector(6.47, -8.04) * mm});
            skLineSegment(sketch, "E262", {"start": v(-97, 4.37) * mm, "end": v(-96.76, 3.7) * mm});
            skLineSegment(sketch, "E263", {"start": v(-96.76, 3.7) * mm, "end": v(-96.76, 1.66) * mm});
            skLineSegment(sketch, "E264", {"start": v(-96.76, 1.66) * mm, "end": v(-97.16, 1.3) * mm});
            skLineSegment(sketch, "E265", {"start": v(-97.16, 1.3) * mm, "end": v(-102.89, 1.3) * mm});
            skLineSegment(sketch, "E266", {"start": v(-95.6, -3.34) * mm, "end": v(-97.37, -3.34) * mm});
            skLineSegment(sketch, "E267", {"start": v(-97.37, -3.34) * mm, "end": v(-97.37, -1.25) * mm});
            skFitSpline(sketch, "E268", {"points": [v(-97.37, -1.25) * mm, v(-97, -0.37) * mm, v(-95.99, 0.09) * mm, v(-95.6, 0.13) * mm], "startDerivative": vector(0.54, 2.62) * mm, "endDerivative": vector(1.39, 0.05) * mm});
            skLineSegment(sketch, "E269.bottom", {"start": v(-96.27, -4.46) * mm, "end": v(-97.93, -4.46) * mm});
            skLineSegment(sketch, "E269.top", {"start": v(-96.27, -9) * mm, "end": v(-97.93, -9) * mm});
            skLineSegment(sketch, "E269.left", {"start": v(-96.27, -4.46) * mm, "end": v(-96.27, -9) * mm});
            skLineSegment(sketch, "E269.right", {"start": v(-97.93, -4.46) * mm, "end": v(-97.93, -9) * mm});
            skLineSegment(sketch, "E270", {"start": v(-100.12, -8.97) * mm, "end": v(-99.05, -8.97) * mm});
            skLineSegment(sketch, "E271", {"start": v(-99.05, -8.97) * mm, "end": v(-99.05, -5.51) * mm});
            skLineSegment(sketch, "E272", {"start": v(-99.05, -5.51) * mm, "end": v(-100.19, -6.73) * mm});
            skLineSegment(sketch, "E273", {"start": v(-100.19, -6.73) * mm, "end": v(-100.12, -8.97) * mm});
            skCircle(sketch, "E274", {"center": v(-102.5, -8.92) * mm, "radius": 0.94 * mm});
            skLineSegment(sketch, "E275.MirrorCS", {"start": v(-95.6, 18.35) * mm, "end": v(-92.43, 18.35) * mm});
            skFitSpline(sketch, "E276.MirrorCS", {"points": [v(-92.43, 18.35) * mm, v(-89.2, 17.41) * mm, v(-86.3, 15.23) * mm, v(-84.37, 11.85) * mm, v(-84.05, 10.34) * mm], "startDerivative": vector(12.5, -2.75) * mm, "endDerivative": vector(0.88, -7.56) * mm});
            skLineSegment(sketch, "E277.MirrorCS", {"start": v(-84.05, 10.34) * mm, "end": v(-84.05, 5.14) * mm});
            skLineSegment(sketch, "E278.MirrorCS", {"start": v(-84.05, 5.14) * mm, "end": v(-79.53, -6.62) * mm});
            skFitSpline(sketch, "E279.MirrorCS", {"points": [v(-79.53, -6.62) * mm, v(-80.2, -8.13) * mm, v(-83.17, -10.52) * mm, v(-87.38, -12.19) * mm, v(-93.94, -13.43) * mm, v(-95.6, -13.54) * mm], "startDerivative": vector(-3, -10.53) * mm, "endDerivative": vector(-9.52, -0.14) * mm});
            skLineSegment(sketch, "E280.MirrorCS", {"start": v(-81.29, -6.58) * mm, "end": v(-85.62, 4.37) * mm});
            skLineSegment(sketch, "E281.MirrorCS", {"start": v(-82.37, -6.95) * mm, "end": v(-87.1, 4.9) * mm});
            skArc(sketch, "E282.MirrorCS", {"start": v(-81.29, -6.58) * mm, "mid": v(-81.66, -7.25) * mm, "end": v(-82.37, -6.95) * mm});
            skCircle(sketch, "E283.MirrorC", {"center": v(-88.7, -8.92) * mm, "radius": 0.94 * mm});
            skLineSegment(sketch, "E284.MirrorCS", {"start": v(-91.01, -6.73) * mm, "end": v(-91.08, -8.97) * mm});
            skLineSegment(sketch, "E285.MirrorCS", {"start": v(-91.08, -8.97) * mm, "end": v(-92.15, -8.97) * mm});
            skLineSegment(sketch, "E286.MirrorCS", {"start": v(-92.15, -8.97) * mm, "end": v(-92.15, -5.51) * mm});
            skLineSegment(sketch, "E287.MirrorCS", {"start": v(-92.15, -5.51) * mm, "end": v(-91.01, -6.73) * mm});
            skLineSegment(sketch, "E288.MirrorCS", {"start": v(-93.27, -4.46) * mm, "end": v(-93.27, -9) * mm});
            skLineSegment(sketch, "E289.MirrorCS", {"start": v(-94.93, -4.46) * mm, "end": v(-93.27, -4.46) * mm});
            skLineSegment(sketch, "E290.MirrorCS", {"start": v(-94.93, -4.46) * mm, "end": v(-94.93, -9) * mm});
            skLineSegment(sketch, "E291.MirrorCS", {"start": v(-94.93, -9) * mm, "end": v(-93.27, -9) * mm});
            skLineSegment(sketch, "E292.MirrorCS", {"start": v(-93.83, -3.34) * mm, "end": v(-93.83, -1.25) * mm});
            skLineSegment(sketch, "E293.MirrorCS", {"start": v(-95.6, -3.34) * mm, "end": v(-93.83, -3.34) * mm});
            skFitSpline(sketch, "E294.MirrorCS", {"points": [v(-93.83, -1.25) * mm, v(-94.2, -0.37) * mm, v(-95.21, 0.09) * mm, v(-95.6, 0.13) * mm], "startDerivative": vector(-0.54, 2.62) * mm, "endDerivative": vector(-1.39, 0.05) * mm});
            skLineSegment(sketch, "E295.MirrorCS", {"start": v(-94.04, 1.3) * mm, "end": v(-88.31, 1.3) * mm});
            skLineSegment(sketch, "E296.MirrorCS", {"start": v(-94.44, 3.7) * mm, "end": v(-94.44, 1.66) * mm});
            skLineSegment(sketch, "E297.MirrorCS", {"start": v(-94.44, 1.66) * mm, "end": v(-94.04, 1.3) * mm});
            skFitSpline(sketch, "E298.MirrorCS", {"points": [v(-88.31, 1.3) * mm, v(-87.57, 2.04) * mm, v(-87.85, 3.7) * mm, v(-89.3, 5.22) * mm, v(-91.28, 5.78) * mm, v(-93.02, 5.5) * mm, v(-94.2, 4.37) * mm], "startDerivative": vector(7.07, 4.58) * mm, "endDerivative": vector(-6.47, -8.04) * mm});
            skLineSegment(sketch, "E299.MirrorCS", {"start": v(-94.2, 4.37) * mm, "end": v(-94.44, 3.7) * mm});
            skFitSpline(sketch, "E300.MirrorCS", {"points": [v(-87.1, 4.9) * mm, v(-88.43, 6.72) * mm, v(-91.12, 7.62) * mm, v(-93.38, 7.03) * mm, v(-94.77, 6.3) * mm], "startDerivative": vector(-4.2, 7.92) * mm, "endDerivative": vector(-6.2, -3.55) * mm});
            skFitSpline(sketch, "E301.MirrorCS", {"points": [v(-94.77, 6.3) * mm, v(-95.15, 6.06) * mm, v(-95.6, 6.02) * mm], "startDerivative": vector(-0.72, -0.55) * mm, "endDerivative": vector(-0.93, 0.02) * mm});
            skFitSpline(sketch, "E302.MirrorCS", {"points": [v(-85.62, 4.37) * mm, v(-86.98, 6.79) * mm, v(-89.33, 8.36) * mm, v(-91.5, 8.61) * mm, v(-93.1, 8.3) * mm, v(-94.25, 7.74) * mm, v(-95.6, 7.06) * mm], "startDerivative": vector(-5.68, 13) * mm, "endDerivative": vector(-9.61, -4.7) * mm});
            skSolve(sketch);
        }
        {
            var Q0;
            Q0=qCreatedBy(makeId("Top.planeOp"),FACE);
            var sketch = newSketch(context, id + "F5", { "sketchPlane" : qUnion([Q0])});
            skLineSegment(sketch, "E303", {"start": v(-22.97, 23.67) * mm, "end": v(-33.62, 23.67) * mm});
            skLineSegment(sketch, "E304", {"start": v(-33.62, 23.67) * mm, "end": v(-44.32, 5.17) * mm});
            skLineSegment(sketch, "E305", {"start": v(-44.32, 5.17) * mm, "end": v(-33.62, -13.33) * mm});
            skLineSegment(sketch, "E306", {"start": v(-33.62, -13.33) * mm, "end": v(-22.97, -13.33) * mm});
            skLineSegment(sketch, "E307.0", {"start": v(-25.64, -1.03) * mm, "end": v(-22.97, -1.03) * mm});
            skLineSegment(sketch, "E307.1", {"start": v(-29.59, 4.26) * mm, "end": v(-26.96, -0.28) * mm});
            skLineSegment(sketch, "E307.2", {"start": v(-26.96, 10.6) * mm, "end": v(-29.56, 6.13) * mm});
            skLineSegment(sketch, "E307.3", {"start": v(-22.97, 11.37) * mm, "end": v(-25.64, 11.37) * mm});
            skLineSegment(sketch, "E308.0", {"start": v(-31.2, -10.63) * mm, "end": v(-22.97, -10.63) * mm});
            skLineSegment(sketch, "E308.1", {"start": v(-40.68, 4.26) * mm, "end": v(-32.51, -9.86) * mm});
            skLineSegment(sketch, "E308.2", {"start": v(-32.51, 20.2) * mm, "end": v(-40.64, 6.13) * mm});
            skLineSegment(sketch, "E308.3", {"start": v(-22.97, 20.97) * mm, "end": v(-31.2, 20.97) * mm});
            skLineSegment(sketch, "E309", {"start": v(-31.2, 20.97) * mm, "end": v(-25.64, 11.37) * mm});
            skLineSegment(sketch, "E310", {"start": v(-32.51, 20.2) * mm, "end": v(-26.96, 10.6) * mm});
            skLineSegment(sketch, "E311", {"start": v(-40.64, 6.13) * mm, "end": v(-29.56, 6.13) * mm});
            skLineSegment(sketch, "E312", {"start": v(-40.68, 4.26) * mm, "end": v(-29.59, 4.26) * mm});
            skLineSegment(sketch, "E313.MirrorCS", {"start": v(-31.2, -10.63) * mm, "end": v(-25.64, -1.03) * mm});
            skLineSegment(sketch, "E314.MirrorCS", {"start": v(-32.51, -9.86) * mm, "end": v(-26.96, -0.28) * mm});
            skLineSegment(sketch, "E315.MirrorCS", {"start": v(-22.97, 20.97) * mm, "end": v(-14.75, 20.97) * mm});
            skLineSegment(sketch, "E316.MirrorCS", {"start": v(-14.75, 20.97) * mm, "end": v(-20.3, 11.37) * mm});
            skLineSegment(sketch, "E317.MirrorCS", {"start": v(-13.44, 20.2) * mm, "end": v(-18.98, 10.6) * mm});
            skLineSegment(sketch, "E318.MirrorCS", {"start": v(-13.44, 20.2) * mm, "end": v(-5.3, 6.13) * mm});
            skLineSegment(sketch, "E319.MirrorCS", {"start": v(-5.3, 6.13) * mm, "end": v(-16.4, 6.13) * mm});
            skLineSegment(sketch, "E320.MirrorCS", {"start": v(-5.27, 4.26) * mm, "end": v(-16.36, 4.26) * mm});
            skLineSegment(sketch, "E321.MirrorCS", {"start": v(-5.27, 4.26) * mm, "end": v(-13.44, -9.86) * mm});
            skLineSegment(sketch, "E322.MirrorCS", {"start": v(-13.44, -9.86) * mm, "end": v(-18.98, -0.28) * mm});
            skLineSegment(sketch, "E323.MirrorCS", {"start": v(-16.36, 4.26) * mm, "end": v(-18.98, -0.28) * mm});
            skLineSegment(sketch, "E324.MirrorCS", {"start": v(-14.75, -10.63) * mm, "end": v(-20.3, -1.03) * mm});
            skLineSegment(sketch, "E325.MirrorCS", {"start": v(-20.3, -1.03) * mm, "end": v(-22.97, -1.03) * mm});
            skLineSegment(sketch, "E326.MirrorCS", {"start": v(-14.75, -10.63) * mm, "end": v(-22.97, -10.63) * mm});
            skLineSegment(sketch, "E327.MirrorCS", {"start": v(-22.97, 11.37) * mm, "end": v(-20.3, 11.37) * mm});
            skLineSegment(sketch, "E328.MirrorCS", {"start": v(-22.97, 23.67) * mm, "end": v(-12.33, 23.67) * mm});
            skLineSegment(sketch, "E329.MirrorCS", {"start": v(-12.33, 23.67) * mm, "end": v(-1.63, 5.17) * mm});
            skLineSegment(sketch, "E330.MirrorCS", {"start": v(-1.63, 5.17) * mm, "end": v(-12.33, -13.33) * mm});
            skLineSegment(sketch, "E331.MirrorCS", {"start": v(-12.33, -13.33) * mm, "end": v(-22.97, -13.33) * mm});
            skLineSegment(sketch, "E332", {"start": v(-18.98, 10.6) * mm, "end": v(-16.4, 6.13) * mm});
            skArc(sketch, "E333", {"start": v(-17.47, 23.67) * mm, "mid": v(-22.97, 29.17) * mm, "end": v(-28.47, 23.67) * mm});
            skCircle(sketch, "E334", {"center": v(-22.97, 26.11) * mm, "radius": 1.59 * mm});
            skSolve(sketch);
        }
        {
            var Q0;
            Q0=qCreatedBy(makeId("Top.planeOp"),FACE);
            var sketch = newSketch(context, id + "F6", { "sketchPlane" : qUnion([Q0])});
            skCircle(sketch, "E335", {"center": v(46.93, 6.07) * mm, "radius": 20 * mm});
            skPoint(sketch, "E336.startSnap0", {"position": v(46.93, 24.95) * mm});
            skLineSegment(sketch, "E337", {"start": v(46.93, 20.6) * mm, "end": v(45.69, 0) * mm});
            skLineSegment(sketch, "E338", {"start": v(45.69, 0) * mm, "end": v(44.05, 1.78) * mm});
            skLineSegment(sketch, "E339", {"start": v(44.05, 1.78) * mm, "end": v(45.18, -1.7) * mm});
            skLineSegment(sketch, "E340", {"start": v(45.18, -1.7) * mm, "end": v(41.57, -2.54) * mm});
            skLineSegment(sketch, "E341", {"start": v(41.57, -2.54) * mm, "end": v(45.07, -3.57) * mm});
            skLineSegment(sketch, "E342", {"start": v(45.07, -3.57) * mm, "end": v(44.09, -5.91) * mm});
            skLineSegment(sketch, "E343", {"start": v(44.09, -5.91) * mm, "end": v(45.9, -4.68) * mm});
            skLineSegment(sketch, "E344", {"start": v(45.9, -4.68) * mm, "end": v(45.9, -9.6) * mm});
            skFitSpline(sketch, "E345", {"points": [v(45.9, -9.6) * mm, v(43.84, -8.9) * mm, v(40.35, -6.03) * mm, v(37.78, -1.14) * mm, v(37.75, 4.61) * mm, v(39.23, 8.87) * mm], "startDerivative": vector(-13.93, 3.23) * mm, "endDerivative": vector(8.5, 19.85) * mm});
            skFitSpline(sketch, "E346", {"points": [v(39.23, 8.87) * mm, v(39.23, 9.55) * mm, v(37.77, 11.8) * mm, v(36.25, 14.93) * mm, v(35.73, 18) * mm, v(36.5, 21.42) * mm, v(38.23, 24.08) * mm], "startDerivative": vector(1.57, 7.16) * mm, "endDerivative": vector(10.46, 13.64) * mm});
            skFitSpline(sketch, "E347", {"points": [v(37.08, 23.48) * mm, v(34.97, 21) * mm, v(33.2, 18.75) * mm, v(31.71, 15.11) * mm, v(31.29, 9.82) * mm, v(32.82, 4.84) * mm, v(33.51, 3.31) * mm, v(33.46, 2.8) * mm, v(32.97, 2.89) * mm, v(32.2, 3.82) * mm, v(30.13, 7.8) * mm, v(29.95, 13.45) * mm, v(29.94, 14.88) * mm], "startDerivative": vector(-23.26, -27.54) * mm, "endDerivative": vector(-1.03, 18.96) * mm});
            skFitSpline(sketch, "E348", {"points": [v(29.94, 14.88) * mm, v(29.33, 13.73) * mm, v(28.51, 11.04) * mm, v(28.47, 7.16) * mm, v(28.76, 3.85) * mm, v(30.25, 0.44) * mm, v(31.55, -1.7) * mm, v(31.75, -2.06) * mm, v(31.4, -2.2) * mm, v(30.83, -1.7) * mm, v(28.43, 1.94) * mm], "startDerivative": vector(-7.54, -12.9) * mm, "endDerivative": vector(-19.37, 30.06) * mm});
            skFitSpline(sketch, "E349", {"points": [v(28.43, 1.94) * mm, v(28.43, 1.25) * mm, v(29.36, -0.96) * mm, v(30.94, -3.72) * mm, v(36.03, -8.83) * mm, v(40.92, -11.13) * mm, v(46.93, -12.07) * mm], "startDerivative": vector(-1.3, -8.35) * mm, "endDerivative": vector(29.52, -3.3) * mm});
            skLineSegment(sketch, "E350.MirrorCS", {"start": v(46.93, 20.6) * mm, "end": v(48.17, 0) * mm});
            skLineSegment(sketch, "E351.MirrorCS", {"start": v(48.17, 0) * mm, "end": v(49.81, 1.78) * mm});
            skLineSegment(sketch, "E352.MirrorCS", {"start": v(49.81, 1.78) * mm, "end": v(48.68, -1.7) * mm});
            skLineSegment(sketch, "E353.MirrorCS", {"start": v(48.68, -1.7) * mm, "end": v(52.3, -2.54) * mm});
            skLineSegment(sketch, "E354.MirrorCS", {"start": v(48.8, -3.57) * mm, "end": v(49.77, -5.91) * mm});
            skLineSegment(sketch, "E355.MirrorCS", {"start": v(49.77, -5.91) * mm, "end": v(47.95, -4.68) * mm});
            skLineSegment(sketch, "E356.MirrorCS", {"start": v(47.95, -4.68) * mm, "end": v(47.95, -9.6) * mm});
            skFitSpline(sketch, "E357.MirrorCS", {"points": [v(47.95, -9.6) * mm, v(50.02, -8.9) * mm, v(53.51, -6.03) * mm, v(56.09, -1.14) * mm, v(56.11, 4.61) * mm, v(54.64, 8.87) * mm], "startDerivative": vector(13.93, 3.23) * mm, "endDerivative": vector(-8.5, 19.85) * mm});
            skLineSegment(sketch, "E358.MirrorCS", {"start": v(52.3, -2.54) * mm, "end": v(48.8, -3.57) * mm});
            skFitSpline(sketch, "E359.MirrorCS", {"points": [v(56.78, 23.48) * mm, v(58.89, 21) * mm, v(60.67, 18.75) * mm, v(62.15, 15.11) * mm, v(62.57, 9.82) * mm, v(61.04, 4.84) * mm, v(60.35, 3.31) * mm, v(60.4, 2.8) * mm, v(60.9, 2.89) * mm, v(61.66, 3.82) * mm, v(63.73, 7.8) * mm, v(63.9, 13.45) * mm, v(63.92, 14.88) * mm], "startDerivative": vector(23.26, -27.54) * mm, "endDerivative": vector(1.03, 18.96) * mm});
            skFitSpline(sketch, "E360.MirrorCS", {"points": [v(63.92, 14.88) * mm, v(64.54, 13.73) * mm, v(65.35, 11.04) * mm, v(65.4, 7.16) * mm, v(65.1, 3.85) * mm, v(63.61, 0.44) * mm, v(62.31, -1.7) * mm, v(62.1, -2.06) * mm, v(62.47, -2.2) * mm, v(63.03, -1.7) * mm, v(65.44, 1.94) * mm], "startDerivative": vector(7.54, -12.9) * mm, "endDerivative": vector(19.37, 30.06) * mm});
            skFitSpline(sketch, "E361.MirrorCS", {"points": [v(65.44, 1.94) * mm, v(65.44, 1.25) * mm, v(64.5, -0.96) * mm, v(62.92, -3.72) * mm, v(57.83, -8.83) * mm, v(52.94, -11.13) * mm, v(46.93, -12.07) * mm], "startDerivative": vector(1.3, -8.35) * mm, "endDerivative": vector(-29.52, -3.3) * mm});
            skFitSpline(sketch, "E362.MirrorCS", {"points": [v(54.64, 8.87) * mm, v(54.64, 9.55) * mm, v(56.1, 11.8) * mm, v(57.6, 14.93) * mm, v(58.13, 18) * mm, v(57.35, 21.42) * mm, v(55.63, 24.08) * mm], "startDerivative": vector(-1.57, 7.16) * mm, "endDerivative": vector(-10.46, 13.64) * mm});
            skArc(sketch, "E363", {"start": v(46.93, 20.57) * mm, "mid": v(46.93, 20.57) * mm, "end": v(46.93, 20.57) * mm});
            skCircle(sketch, "E364", {"center": v(46.93, 28.67) * mm, "radius": 1.59 * mm});
            skArc(sketch, "E365.trimOffspring", {"start": v(52.25, 27.49) * mm, "mid": v(46.93, 31.57) * mm, "end": v(41.61, 27.49) * mm});
            skLineSegment(sketch, "E366", {"start": v(35.71, 21.86) * mm, "end": v(37.86, 23.6) * mm});
            skLineSegment(sketch, "E367.MirrorCS", {"start": v(58.15, 21.86) * mm, "end": v(56, 23.6) * mm});
            skArc(sketch, "E368", {"start": v(41.61, 27.49) * mm, "mid": v(46.93, -15.99) * mm, "end": v(52.25, 27.49) * mm});
            skSolve(sketch);
        }
        {
            var Q0;
            Q0=qCreatedBy(makeId("Top.planeOp"),FACE);
            var sketch = newSketch(context, id + "F7", { "sketchPlane" : qUnion([Q0])});
            skCircle(sketch, "E369", {"center": v(97.23, 7.38) * mm, "radius": 18.5 * mm});
            skArc(sketch, "E370", {"start": v(93.1, 3.82) * mm, "mid": v(94.45, 2.7) * mm, "end": v(96.08, 2.06) * mm});
            skLineSegment(sketch, "E371", {"start": v(96.08, 12.71) * mm, "end": v(95.18, 18.26) * mm});
            skLineSegment(sketch, "E372", {"start": v(95.18, 18.26) * mm, "end": v(97.23, 18.26) * mm});
            skLineSegment(sketch, "E373", {"start": v(93.1, 10.95) * mm, "end": v(88.86, 14.66) * mm});
            skLineSegment(sketch, "E374", {"start": v(88.86, 14.66) * mm, "end": v(86.72, 10.94) * mm});
            skLineSegment(sketch, "E375", {"start": v(86.72, 10.94) * mm, "end": v(92.01, 8.97) * mm});
            skArc(sketch, "E376", {"start": v(87.1, 18) * mm, "mid": v(85.92, 16.72) * mm, "end": v(84.9, 15.32) * mm});
            skArc(sketch, "E377", {"start": v(96.35, 23.94) * mm, "mid": v(88.85, 21.7) * mm, "end": v(83.22, 16.25) * mm});
            skLineSegment(sketch, "E378", {"start": v(96.35, 23.94) * mm, "end": v(96.35, 22.02) * mm});
            skLineSegment(sketch, "E379", {"start": v(83.22, 16.25) * mm, "end": v(84.9, 15.32) * mm});
            skLineSegment(sketch, "E380", {"start": v(82.25, 14.5) * mm, "end": v(83.93, 13.56) * mm});
            skArc(sketch, "E381", {"start": v(93.83, 19.59) * mm, "mid": v(90.97, 18.4) * mm, "end": v(88.5, 16.56) * mm});
            skLineSegment(sketch, "E382", {"start": v(87.1, 18) * mm, "end": v(88.5, 16.56) * mm});
            skLineSegment(sketch, "E383", {"start": v(83.03, 11.03) * mm, "end": v(84.95, 10.5) * mm});
            skLineSegment(sketch, "E384", {"start": v(93.26, 21.5) * mm, "end": v(93.83, 19.59) * mm});
            skLineSegment(sketch, "E385.MirrorCS", {"start": v(98.1, 23.94) * mm, "end": v(98.1, 22.02) * mm});
            skLineSegment(sketch, "E386.MirrorCS", {"start": v(101.2, 21.5) * mm, "end": v(100.62, 19.59) * mm});
            skLineSegment(sketch, "E387.MirrorCS", {"start": v(107.35, 18) * mm, "end": v(105.96, 16.56) * mm});
            skLineSegment(sketch, "E388.MirrorCS", {"start": v(111.43, 11.03) * mm, "end": v(109.5, 10.5) * mm});
            skLineSegment(sketch, "E389.MirrorCS", {"start": v(112.2, 14.5) * mm, "end": v(110.53, 13.56) * mm});
            skLineSegment(sketch, "E390.MirrorCS", {"start": v(111.24, 16.25) * mm, "end": v(109.56, 15.32) * mm});
            skLineSegment(sketch, "E391.MirrorCS", {"start": v(98.37, 12.71) * mm, "end": v(99.27, 18.26) * mm});
            skLineSegment(sketch, "E392.MirrorCS", {"start": v(99.27, 18.26) * mm, "end": v(97.23, 18.26) * mm});
            skLineSegment(sketch, "E393.MirrorCS", {"start": v(101.35, 10.95) * mm, "end": v(105.59, 14.66) * mm});
            skLineSegment(sketch, "E394.MirrorCS", {"start": v(107.73, 10.94) * mm, "end": v(102.44, 8.97) * mm});
            skLineSegment(sketch, "E395.MirrorCS", {"start": v(105.59, 14.66) * mm, "end": v(107.73, 10.94) * mm});
            skLineSegment(sketch, "E396.MirrorCS", {"start": v(86.72, 3.83) * mm, "end": v(92.01, 5.8) * mm});
            skLineSegment(sketch, "E397.MirrorCS", {"start": v(88.86, 0.1) * mm, "end": v(86.72, 3.83) * mm});
            skLineSegment(sketch, "E398.MirrorCS", {"start": v(93.1, 3.82) * mm, "end": v(88.86, 0.1) * mm});
            skLineSegment(sketch, "E399.MirrorCS", {"start": v(96.08, 2.06) * mm, "end": v(95.18, -3.5) * mm});
            skLineSegment(sketch, "E400.MirrorCS", {"start": v(95.18, -3.5) * mm, "end": v(97.23, -3.5) * mm});
            skLineSegment(sketch, "E401.MirrorCS", {"start": v(99.27, -3.5) * mm, "end": v(97.23, -3.5) * mm});
            skLineSegment(sketch, "E402.MirrorCS", {"start": v(98.37, 2.06) * mm, "end": v(99.27, -3.5) * mm});
            skLineSegment(sketch, "E403.MirrorCS", {"start": v(101.35, 3.82) * mm, "end": v(105.59, 0.1) * mm});
            skLineSegment(sketch, "E404.MirrorCS", {"start": v(105.59, 0.1) * mm, "end": v(107.73, 3.83) * mm});
            skLineSegment(sketch, "E405.MirrorCS", {"start": v(107.73, 3.83) * mm, "end": v(102.44, 5.8) * mm});
            skLineSegment(sketch, "E406.MirrorCS", {"start": v(101.2, -6.73) * mm, "end": v(100.62, -4.82) * mm});
            skLineSegment(sketch, "E407.MirrorCS", {"start": v(93.26, -6.73) * mm, "end": v(93.83, -4.82) * mm});
            skLineSegment(sketch, "E408.MirrorCS", {"start": v(87.1, -3.22) * mm, "end": v(88.5, -1.79) * mm});
            skLineSegment(sketch, "E409.MirrorCS", {"start": v(83.03, 3.74) * mm, "end": v(84.95, 4.28) * mm});
            skLineSegment(sketch, "E410.MirrorCS", {"start": v(107.35, -3.22) * mm, "end": v(105.96, -1.79) * mm});
            skLineSegment(sketch, "E411.MirrorCS", {"start": v(111.43, 3.74) * mm, "end": v(109.5, 4.28) * mm});
            skLineSegment(sketch, "E412.MirrorCS", {"start": v(82.25, 0.28) * mm, "end": v(83.93, 1.21) * mm});
            skLineSegment(sketch, "E413.MirrorCS", {"start": v(83.22, -1.48) * mm, "end": v(84.9, -0.55) * mm});
            skLineSegment(sketch, "E414.MirrorCS", {"start": v(111.24, -1.48) * mm, "end": v(109.56, -0.55) * mm});
            skLineSegment(sketch, "E415.MirrorCS", {"start": v(112.2, 0.28) * mm, "end": v(110.53, 1.21) * mm});
            skLineSegment(sketch, "E416.MirrorCS", {"start": v(98.1, -9.17) * mm, "end": v(98.1, -7.25) * mm});
            skLineSegment(sketch, "E417.MirrorCS", {"start": v(96.35, -9.17) * mm, "end": v(96.35, -7.25) * mm});
            skArc(sketch, "E418.trimOffspring", {"start": v(83.03, 3.74) * mm, "mid": v(83.42, 2.45) * mm, "end": v(83.93, 1.21) * mm});
            skArc(sketch, "E419.trimOffspring", {"start": v(93.26, -6.73) * mm, "mid": v(94.8, -7.07) * mm, "end": v(96.35, -7.25) * mm});
            skArc(sketch, "E420.trimOffspring", {"start": v(107.35, -3.22) * mm, "mid": v(108.53, -1.95) * mm, "end": v(109.56, -0.55) * mm});
            skArc(sketch, "E421.trimOffspring", {"start": v(111.43, 11.03) * mm, "mid": v(111.03, 12.32) * mm, "end": v(110.53, 13.56) * mm});
            skArc(sketch, "E422.trimOffspring", {"start": v(101.2, 21.5) * mm, "mid": v(99.66, 21.84) * mm, "end": v(98.1, 22.02) * mm});
            skArc(sketch, "E423.trimOffspring", {"start": v(96.35, 22.02) * mm, "mid": v(94.8, 21.84) * mm, "end": v(93.26, 21.5) * mm});
            skArc(sketch, "E424.trimOffspring", {"start": v(82.25, 14.5) * mm, "mid": v(80.65, 7.38) * mm, "end": v(82.25, 0.28) * mm});
            skArc(sketch, "E425.trimOffspring", {"start": v(83.93, 13.56) * mm, "mid": v(83.42, 12.32) * mm, "end": v(83.03, 11.03) * mm});
            skArc(sketch, "E426.trimOffspring", {"start": v(84.95, 10.5) * mm, "mid": v(84.56, 7.38) * mm, "end": v(84.95, 4.28) * mm});
            skArc(sketch, "E427.trimOffspring", {"start": v(83.22, -1.48) * mm, "mid": v(88.85, -6.92) * mm, "end": v(96.35, -9.17) * mm});
            skArc(sketch, "E428.trimOffspring", {"start": v(84.9, -0.55) * mm, "mid": v(85.92, -1.95) * mm, "end": v(87.1, -3.22) * mm});
            skArc(sketch, "E429.trimOffspring", {"start": v(88.5, -1.79) * mm, "mid": v(90.97, -3.63) * mm, "end": v(93.83, -4.82) * mm});
            skArc(sketch, "E430.trimOffspring", {"start": v(111.24, 16.25) * mm, "mid": v(105.6, 21.7) * mm, "end": v(98.1, 23.94) * mm});
            skArc(sketch, "E431.trimOffspring", {"start": v(109.56, 15.32) * mm, "mid": v(108.53, 16.72) * mm, "end": v(107.35, 18) * mm});
            skArc(sketch, "E432.trimOffspring", {"start": v(105.96, 16.56) * mm, "mid": v(103.48, 18.4) * mm, "end": v(100.62, 19.59) * mm});
            skArc(sketch, "E433.trimOffspring", {"start": v(112.2, 0.28) * mm, "mid": v(113.8, 7.38) * mm, "end": v(112.2, 14.5) * mm});
            skArc(sketch, "E434.trimOffspring", {"start": v(110.53, 1.21) * mm, "mid": v(111.03, 2.45) * mm, "end": v(111.43, 3.74) * mm});
            skArc(sketch, "E435.trimOffspring", {"start": v(109.5, 4.28) * mm, "mid": v(109.9, 7.38) * mm, "end": v(109.5, 10.5) * mm});
            skArc(sketch, "E436.trimOffspring", {"start": v(92.01, 8.97) * mm, "mid": v(91.78, 7.38) * mm, "end": v(92.01, 5.8) * mm});
            skArc(sketch, "E437.trimOffspring", {"start": v(96.08, 12.71) * mm, "mid": v(94.45, 12.07) * mm, "end": v(93.1, 10.95) * mm});
            skArc(sketch, "E438.trimOffspring", {"start": v(101.35, 10.95) * mm, "mid": v(100, 12.07) * mm, "end": v(98.37, 12.71) * mm});
            skArc(sketch, "E439.trimOffspring", {"start": v(102.44, 5.8) * mm, "mid": v(102.68, 7.38) * mm, "end": v(102.44, 8.97) * mm});
            skArc(sketch, "E440.trimOffspring", {"start": v(98.1, -7.25) * mm, "mid": v(99.66, -7.07) * mm, "end": v(101.2, -6.73) * mm});
            skArc(sketch, "E441.trimOffspring", {"start": v(98.1, -9.17) * mm, "mid": v(105.6, -6.92) * mm, "end": v(111.24, -1.48) * mm});
            skArc(sketch, "E442.trimOffspring", {"start": v(100.62, -4.82) * mm, "mid": v(103.48, -3.63) * mm, "end": v(105.96, -1.79) * mm});
            skArc(sketch, "E443.trimOffspring", {"start": v(98.37, 2.06) * mm, "mid": v(100, 2.7) * mm, "end": v(101.35, 3.82) * mm});
            skArc(sketch, "E444", {"start": v(102.67, 25.08) * mm, "mid": v(97.23, 31.4) * mm, "end": v(91.79, 25.08) * mm});
            skCircle(sketch, "E445", {"center": v(97.23, 28.41) * mm, "radius": 1.59 * mm});
            skSolve(sketch);
        }
        {
            var Q0;
            Q0=qCreatedBy(makeId("Top.planeOp"),FACE);
            var sketch = newSketch(context, id + "F8", { "sketchPlane" : qUnion([Q0])});
            skArc(sketch, "E446", {"start": v(-101.82, -40.35) * mm, "mid": v(-92.95, -78.28) * mm, "end": v(-84.08, -40.35) * mm});
            skLineSegment(sketch, "E447", {"start": v(-92.95, -38.28) * mm, "end": v(-96.74, -42.41) * mm});
            skFitSpline(sketch, "E448", {"points": [v(-96.74, -42.41) * mm, v(-95.89, -43.4) * mm, v(-95.03, -45.53) * mm, v(-94.83, -47.14) * mm], "startDerivative": vector(3.03, -2.83) * mm, "endDerivative": vector(0.26, -4.68) * mm});
            skFitSpline(sketch, "E449", {"points": [v(-94.83, -47.14) * mm, v(-95.62, -46.02) * mm, v(-97.07, -44.8) * mm, v(-98.25, -44.06) * mm], "startDerivative": vector(-2.15, 3.57) * mm, "endDerivative": vector(-3.59, 2.14) * mm});
            skLineSegment(sketch, "E450", {"start": v(-100.54, -46.55) * mm, "end": v(-100.77, -46.8) * mm});
            skFitSpline(sketch, "E451", {"points": [v(-100.77, -46.8) * mm, v(-99.56, -47.25) * mm, v(-97.56, -48.95) * mm, v(-96.28, -51.48) * mm, v(-95.81, -53.17) * mm, v(-95.67, -56.84) * mm, v(-96.55, -59.46) * mm, v(-98.45, -61.25) * mm, v(-101.34, -61.35) * mm, v(-103.51, -60.21) * mm, v(-105.1, -58.58) * mm, v(-106.4, -56.35) * mm, v(-107.16, -53.86) * mm, v(-107.13, -50.23) * mm, v(-106, -46.58) * mm, v(-104.22, -43.46) * mm, v(-102.82, -41.65) * mm, v(-101.82, -40.35) * mm], "startDerivative": vector(27.44, -8.16) * mm, "endDerivative": vector(20.92, 27.02) * mm});
            skLineSegment(sketch, "E452.MirrorCS", {"start": v(-92.95, -38.28) * mm, "end": v(-89.16, -42.41) * mm});
            skFitSpline(sketch, "E453.MirrorCS", {"points": [v(-89.16, -42.41) * mm, v(-90.02, -43.4) * mm, v(-90.87, -45.53) * mm, v(-91.07, -47.14) * mm], "startDerivative": vector(-3.03, -2.83) * mm, "endDerivative": vector(-0.26, -4.68) * mm});
            skFitSpline(sketch, "E454.MirrorCS", {"points": [v(-91.07, -47.14) * mm, v(-90.28, -46.02) * mm, v(-88.83, -44.8) * mm, v(-87.65, -44.06) * mm], "startDerivative": vector(2.15, 3.57) * mm, "endDerivative": vector(3.59, 2.14) * mm});
            skFitSpline(sketch, "E455.MirrorCS", {"points": [v(-85.14, -46.8) * mm, v(-86.34, -47.25) * mm, v(-88.34, -48.95) * mm, v(-89.63, -51.48) * mm, v(-90.09, -53.17) * mm, v(-90.23, -56.84) * mm, v(-89.35, -59.46) * mm, v(-87.46, -61.25) * mm, v(-84.56, -61.35) * mm, v(-82.4, -60.21) * mm, v(-80.8, -58.58) * mm, v(-79.5, -56.35) * mm, v(-78.74, -53.86) * mm, v(-78.77, -50.23) * mm, v(-79.9, -46.58) * mm, v(-81.68, -43.46) * mm, v(-83.08, -41.65) * mm, v(-84.08, -40.35) * mm], "startDerivative": vector(-27.44, -8.16) * mm, "endDerivative": vector(-20.92, 27.02) * mm});
            skLineSegment(sketch, "E456.trimOffspring", {"start": v(-98.25, -44.06) * mm, "end": v(-100.54, -46.55) * mm});
            skLineSegment(sketch, "E457.trimOffspring", {"start": v(-87.65, -44.06) * mm, "end": v(-85.36, -46.55) * mm});
            skArc(sketch, "E458", {"start": v(-98.4, -77.52) * mm, "mid": v(-92.95, -83.78) * mm, "end": v(-87.5, -77.52) * mm});
            skCircle(sketch, "E459", {"center": v(-92.95, -80.5) * mm, "radius": 1.59 * mm});
            skLineSegment(sketch, "E460", {"start": v(-85.36, -46.55) * mm, "end": v(-85.14, -46.8) * mm});
            skSolve(sketch);
        }
        {
            var Q0;
            Q0=qCreatedBy(makeId("Top.planeOp"),FACE);
            var sketch = newSketch(context, id + "F9", { "sketchPlane" : qUnion([Q0])});
            skCircle(sketch, "E461", {"center": v(-22.37, -59.59) * mm, "radius": 7.93 * mm});
            skCircle(sketch, "E462", {"center": v(-22.37, -59.59) * mm, "radius": 11.1 * mm});
            skArc(sketch, "E463", {"start": v(-35.25, -57.36) * mm, "mid": v(-35.45, -59.59) * mm, "end": v(-35.25, -61.82) * mm});
            skLineSegment(sketch, "E464", {"start": v(-42.37, -39.59) * mm, "end": v(-36.35, -50) * mm});
            skLineSegment(sketch, "E465", {"start": v(-36.35, -50) * mm, "end": v(-41.45, -49.12) * mm});
            skLineSegment(sketch, "E466", {"start": v(-41.45, -49.12) * mm, "end": v(-35.25, -57.36) * mm});
            skLineSegment(sketch, "E467.MirrorCS", {"start": v(-42.37, -39.59) * mm, "end": v(-31.96, -45.61) * mm});
            skLineSegment(sketch, "E468.MirrorCS", {"start": v(-32.85, -40.52) * mm, "end": v(-24.6, -46.7) * mm});
            skLineSegment(sketch, "E469.MirrorCS", {"start": v(-31.96, -45.61) * mm, "end": v(-32.85, -40.52) * mm});
            skLineSegment(sketch, "E470.MirrorCS", {"start": v(-3.3, -70.06) * mm, "end": v(-9.5, -61.82) * mm});
            skLineSegment(sketch, "E471.MirrorCS", {"start": v(-8.4, -69.17) * mm, "end": v(-3.3, -70.06) * mm});
            skLineSegment(sketch, "E472.MirrorCS", {"start": v(-2.37, -79.59) * mm, "end": v(-8.4, -69.17) * mm});
            skLineSegment(sketch, "E473.MirrorCS", {"start": v(-2.37, -79.59) * mm, "end": v(-12.79, -73.56) * mm});
            skLineSegment(sketch, "E474.MirrorCS", {"start": v(-11.9, -78.66) * mm, "end": v(-20.14, -72.47) * mm});
            skLineSegment(sketch, "E475.MirrorCS", {"start": v(-12.79, -73.56) * mm, "end": v(-11.9, -78.66) * mm});
            skLineSegment(sketch, "E476.MirrorCS", {"start": v(-11.9, -40.52) * mm, "end": v(-20.14, -46.7) * mm});
            skLineSegment(sketch, "E477.MirrorCS", {"start": v(-12.79, -45.61) * mm, "end": v(-11.9, -40.52) * mm});
            skLineSegment(sketch, "E478.MirrorCS", {"start": v(-2.37, -39.59) * mm, "end": v(-12.79, -45.61) * mm});
            skLineSegment(sketch, "E479.MirrorCS", {"start": v(-2.37, -39.59) * mm, "end": v(-8.4, -50) * mm});
            skLineSegment(sketch, "E480.MirrorCS", {"start": v(-8.4, -50) * mm, "end": v(-3.3, -49.12) * mm});
            skLineSegment(sketch, "E481.MirrorCS", {"start": v(-3.3, -49.12) * mm, "end": v(-9.5, -57.36) * mm});
            skLineSegment(sketch, "E482.MirrorCS", {"start": v(-32.85, -78.66) * mm, "end": v(-24.6, -72.47) * mm});
            skLineSegment(sketch, "E483.MirrorCS", {"start": v(-31.96, -73.56) * mm, "end": v(-32.85, -78.66) * mm});
            skLineSegment(sketch, "E484.MirrorCS", {"start": v(-42.37, -79.59) * mm, "end": v(-31.96, -73.56) * mm});
            skLineSegment(sketch, "E485.MirrorCS", {"start": v(-36.35, -69.17) * mm, "end": v(-41.45, -70.06) * mm});
            skLineSegment(sketch, "E486.MirrorCS", {"start": v(-41.45, -70.06) * mm, "end": v(-35.25, -61.82) * mm});
            skArc(sketch, "E487.trimOffspring", {"start": v(-20.14, -46.7) * mm, "mid": v(-22.37, -46.52) * mm, "end": v(-24.6, -46.7) * mm});
            skArc(sketch, "E488.trimOffspring", {"start": v(-9.5, -61.82) * mm, "mid": v(-9.3, -59.59) * mm, "end": v(-9.5, -57.36) * mm});
            skArc(sketch, "E489.trimOffspring", {"start": v(-24.6, -72.47) * mm, "mid": v(-22.37, -72.66) * mm, "end": v(-20.14, -72.47) * mm});
            skLineSegment(sketch, "E490", {"start": v(-42.37, -79.59) * mm, "end": v(-36.35, -69.17) * mm});
            skArc(sketch, "E491", {"start": v(-17.93, -41.08) * mm, "mid": v(-22.37, -32.34) * mm, "end": v(-26.82, -41.08) * mm});
            skPoint(sketch, "E491.centerSnap0", {"position": v(-22.37, -46.52) * mm});
            skCircle(sketch, "E492", {"center": v(-22.37, -35.57) * mm, "radius": 1.59 * mm});
            skLineSegment(sketch, "E493", {"start": v(-28.73, -43.61) * mm, "end": v(-26.82, -41.08) * mm});
            skLineSegment(sketch, "E494", {"start": v(-16.02, -43.61) * mm, "end": v(-17.93, -41.08) * mm});
            skSolve(sketch);
        }
        {
            var Q0;
            Q0=qCreatedBy(makeId("Top.planeOp"),FACE);
            var sketch = newSketch(context, id + "F10", { "sketchPlane" : qUnion([Q0])});
            skLineSegment(sketch, "E495", {"start": v(40.46, -49.06) * mm, "end": v(41.36, -48.16) * mm});
            skLineSegment(sketch, "E496", {"start": v(41.36, -48.16) * mm, "end": v(46.09, -52.88) * mm});
            skArc(sketch, "E497", {"start": v(44.28, -54.69) * mm, "mid": v(43.73, -55.72) * mm, "end": v(43.37, -56.83) * mm});
            skArc(sketch, "E498", {"start": v(37.65, -49.26) * mm, "mid": v(35.82, -52.47) * mm, "end": v(34.83, -56.02) * mm});
            skArc(sketch, "E499", {"start": v(36.03, -47.64) * mm, "mid": v(33.72, -51.6) * mm, "end": v(32.54, -56.02) * mm});
            skLineSegment(sketch, "E500", {"start": v(49.6, -45.23) * mm, "end": v(48.23, -45.23) * mm});
            skLineSegment(sketch, "E501", {"start": v(48.23, -45.23) * mm, "end": v(48.23, -51.97) * mm});
            skLineSegment(sketch, "E502", {"start": v(39.04, -44.63) * mm, "end": v(40.66, -46.25) * mm});
            skLineSegment(sketch, "E503", {"start": v(47.42, -41.14) * mm, "end": v(47.42, -43.43) * mm});
            skLineSegment(sketch, "E504.MirrorCS", {"start": v(49.6, -45.23) * mm, "end": v(50.98, -45.23) * mm});
            skLineSegment(sketch, "E505.MirrorCS", {"start": v(50.98, -45.23) * mm, "end": v(50.98, -51.97) * mm});
            skLineSegment(sketch, "E506.MirrorCS", {"start": v(51.79, -41.14) * mm, "end": v(51.79, -43.43) * mm});
            skLineSegment(sketch, "E507.MirrorCS", {"start": v(60.17, -44.63) * mm, "end": v(58.55, -46.25) * mm});
            skLineSegment(sketch, "E508.MirrorCS", {"start": v(57.85, -48.16) * mm, "end": v(53.12, -52.88) * mm});
            skLineSegment(sketch, "E509.MirrorCS", {"start": v(58.75, -49.06) * mm, "end": v(57.85, -48.16) * mm});
            skLineSegment(sketch, "E510.MirrorCS", {"start": v(50.98, -71.18) * mm, "end": v(50.98, -64.44) * mm});
            skLineSegment(sketch, "E511.MirrorCS", {"start": v(48.23, -71.18) * mm, "end": v(48.23, -64.44) * mm});
            skLineSegment(sketch, "E512.MirrorCS", {"start": v(49.6, -71.18) * mm, "end": v(48.23, -71.18) * mm});
            skLineSegment(sketch, "E513.MirrorCS", {"start": v(49.6, -71.18) * mm, "end": v(50.98, -71.18) * mm});
            skLineSegment(sketch, "E514.MirrorCS", {"start": v(41.36, -68.26) * mm, "end": v(46.09, -63.53) * mm});
            skLineSegment(sketch, "E515.MirrorCS", {"start": v(40.46, -67.35) * mm, "end": v(41.36, -68.26) * mm});
            skLineSegment(sketch, "E516.MirrorCS", {"start": v(58.75, -67.35) * mm, "end": v(57.85, -68.26) * mm});
            skLineSegment(sketch, "E517.MirrorCS", {"start": v(57.85, -68.26) * mm, "end": v(53.12, -63.53) * mm});
            skLineSegment(sketch, "E518.MirrorCS", {"start": v(60.17, -71.78) * mm, "end": v(58.55, -70.16) * mm});
            skLineSegment(sketch, "E519.MirrorCS", {"start": v(51.79, -75.27) * mm, "end": v(51.79, -72.98) * mm});
            skLineSegment(sketch, "E520.MirrorCS", {"start": v(47.42, -75.27) * mm, "end": v(47.42, -72.98) * mm});
            skLineSegment(sketch, "E521.MirrorCS", {"start": v(39.04, -71.78) * mm, "end": v(40.66, -70.16) * mm});
            skLineSegment(sketch, "E522.MirrorCS", {"start": v(39.56, -49.96) * mm, "end": v(44.28, -54.69) * mm});
            skLineSegment(sketch, "E523.MirrorCS", {"start": v(40.46, -49.06) * mm, "end": v(39.56, -49.96) * mm});
            skLineSegment(sketch, "E524.MirrorCS", {"start": v(36.03, -47.64) * mm, "end": v(37.65, -49.26) * mm});
            skLineSegment(sketch, "E525.MirrorCS", {"start": v(32.54, -56.02) * mm, "end": v(34.83, -56.02) * mm});
            skLineSegment(sketch, "E526.MirrorCS", {"start": v(36.63, -56.83) * mm, "end": v(43.37, -56.83) * mm});
            skLineSegment(sketch, "E527.MirrorCS", {"start": v(36.63, -58.2) * mm, "end": v(36.63, -56.83) * mm});
            skLineSegment(sketch, "E528.MirrorCS", {"start": v(36.63, -58.2) * mm, "end": v(36.63, -59.58) * mm});
            skLineSegment(sketch, "E529.MirrorCS", {"start": v(39.56, -66.45) * mm, "end": v(44.28, -61.72) * mm});
            skLineSegment(sketch, "E530.MirrorCS", {"start": v(40.46, -67.35) * mm, "end": v(39.56, -66.45) * mm});
            skLineSegment(sketch, "E531.MirrorCS", {"start": v(36.03, -68.77) * mm, "end": v(37.65, -67.15) * mm});
            skLineSegment(sketch, "E532.MirrorCS", {"start": v(32.54, -60.4) * mm, "end": v(34.83, -60.4) * mm});
            skLineSegment(sketch, "E533.MirrorCS", {"start": v(59.65, -49.96) * mm, "end": v(54.93, -54.69) * mm});
            skLineSegment(sketch, "E534.MirrorCS", {"start": v(58.75, -49.06) * mm, "end": v(59.65, -49.96) * mm});
            skLineSegment(sketch, "E535.MirrorCS", {"start": v(63.18, -47.64) * mm, "end": v(61.56, -49.26) * mm});
            skLineSegment(sketch, "E536.MirrorCS", {"start": v(66.67, -56.02) * mm, "end": v(64.38, -56.02) * mm});
            skLineSegment(sketch, "E537.MirrorCS", {"start": v(66.67, -60.4) * mm, "end": v(64.38, -60.4) * mm});
            skLineSegment(sketch, "E538.MirrorCS", {"start": v(63.18, -68.77) * mm, "end": v(61.56, -67.15) * mm});
            skLineSegment(sketch, "E539.MirrorCS", {"start": v(59.65, -66.45) * mm, "end": v(54.93, -61.72) * mm});
            skLineSegment(sketch, "E540.MirrorCS", {"start": v(58.75, -67.35) * mm, "end": v(59.65, -66.45) * mm});
            skLineSegment(sketch, "E541.MirrorCS", {"start": v(62.58, -58.2) * mm, "end": v(62.58, -59.58) * mm});
            skLineSegment(sketch, "E542.MirrorCS", {"start": v(62.58, -58.2) * mm, "end": v(62.58, -56.83) * mm});
            skLineSegment(sketch, "E543.MirrorCS", {"start": v(62.58, -56.83) * mm, "end": v(55.84, -56.83) * mm});
            skLineSegment(sketch, "E544", {"start": v(36.63, -59.58) * mm, "end": v(43.37, -59.58) * mm});
            skLineSegment(sketch, "E545", {"start": v(62.58, -59.58) * mm, "end": v(55.84, -59.58) * mm});
            skArc(sketch, "E546.trimOffspring", {"start": v(48.23, -51.97) * mm, "mid": v(47.12, -52.33) * mm, "end": v(46.09, -52.88) * mm});
            skArc(sketch, "E547.trimOffspring", {"start": v(53.12, -52.88) * mm, "mid": v(52.1, -52.33) * mm, "end": v(50.98, -51.97) * mm});
            skArc(sketch, "E548.trimOffspring", {"start": v(55.84, -56.83) * mm, "mid": v(55.48, -55.72) * mm, "end": v(54.93, -54.69) * mm});
            skArc(sketch, "E549.trimOffspring", {"start": v(54.93, -61.72) * mm, "mid": v(55.48, -60.7) * mm, "end": v(55.84, -59.58) * mm});
            skArc(sketch, "E550.trimOffspring", {"start": v(50.98, -64.44) * mm, "mid": v(52.1, -64.08) * mm, "end": v(53.12, -63.53) * mm});
            skArc(sketch, "E551.trimOffspring", {"start": v(46.09, -63.53) * mm, "mid": v(47.12, -64.08) * mm, "end": v(48.23, -64.44) * mm});
            skArc(sketch, "E552.trimOffspring", {"start": v(43.37, -59.58) * mm, "mid": v(43.73, -60.7) * mm, "end": v(44.28, -61.72) * mm});
            skArc(sketch, "E553.trimOffspring", {"start": v(34.83, -60.4) * mm, "mid": v(35.82, -63.95) * mm, "end": v(37.65, -67.15) * mm});
            skArc(sketch, "E554.trimOffspring", {"start": v(32.54, -60.4) * mm, "mid": v(33.72, -64.82) * mm, "end": v(36.03, -68.77) * mm});
            skArc(sketch, "E555.trimOffspring", {"start": v(40.66, -70.16) * mm, "mid": v(43.86, -72) * mm, "end": v(47.42, -72.98) * mm});
            skArc(sketch, "E556.trimOffspring", {"start": v(39.04, -71.78) * mm, "mid": v(43, -74.1) * mm, "end": v(47.42, -75.27) * mm});
            skArc(sketch, "E557.trimOffspring", {"start": v(51.79, -72.98) * mm, "mid": v(55.35, -72) * mm, "end": v(58.55, -70.16) * mm});
            skArc(sketch, "E558.trimOffspring", {"start": v(51.79, -75.27) * mm, "mid": v(56.21, -74.1) * mm, "end": v(60.17, -71.78) * mm});
            skArc(sketch, "E559.trimOffspring", {"start": v(61.56, -67.15) * mm, "mid": v(63.4, -63.95) * mm, "end": v(64.38, -60.4) * mm});
            skArc(sketch, "E560.trimOffspring", {"start": v(63.18, -68.77) * mm, "mid": v(65.49, -64.82) * mm, "end": v(66.67, -60.4) * mm});
            skArc(sketch, "E561.trimOffspring", {"start": v(64.38, -56.02) * mm, "mid": v(63.4, -52.47) * mm, "end": v(61.56, -49.26) * mm});
            skArc(sketch, "E562.trimOffspring", {"start": v(66.67, -56.02) * mm, "mid": v(65.49, -51.6) * mm, "end": v(63.18, -47.64) * mm});
            skArc(sketch, "E563.trimOffspring", {"start": v(58.55, -46.25) * mm, "mid": v(55.35, -44.42) * mm, "end": v(51.79, -43.43) * mm});
            skArc(sketch, "E564.trimOffspring", {"start": v(60.17, -44.63) * mm, "mid": v(56.21, -42.32) * mm, "end": v(51.79, -41.14) * mm});
            skArc(sketch, "E565.trimOffspring", {"start": v(47.42, -43.43) * mm, "mid": v(43.86, -44.42) * mm, "end": v(40.66, -46.25) * mm});
            skArc(sketch, "E566.trimOffspring", {"start": v(47.42, -41.14) * mm, "mid": v(43, -42.32) * mm, "end": v(39.04, -44.63) * mm});
            skCircle(sketch, "E567", {"center": v(49.6, -58.2) * mm, "radius": 18.54 * mm});
            skArc(sketch, "E568", {"start": v(44.16, -38.97) * mm, "mid": v(49.6, -78.2) * mm, "end": v(55.05, -38.97) * mm});
            skArc(sketch, "E569", {"start": v(55.05, -38.97) * mm, "mid": v(49.6, -32.72) * mm, "end": v(44.16, -38.97) * mm});
            skCircle(sketch, "E570", {"center": v(49.6, -35.62) * mm, "radius": 1.59 * mm});
            skSolve(sketch);
        }
        {
            var Q0;
            Q0=makeQuery(id+"F0.imprint","IMPRINT",FACE,{"disambiguationData":[TD([[makeQuery(id+"F0.imprint","IMPRINT",EDGE,{"derivedFrom":sQuery(id+"F0.wireOp",EDGE,"E3")}),-1.0]])]});
            var Q1;
            {var subQ0=sQuery(id+"F0.wireOp",EDGE,"E1");Q1=makeQuery(id+"F0.imprint","IMPRINT",FACE,{"disambiguationData":[TD([[makeQuery(id+"F0.imprint","IMPRINT",EDGE,{"derivedFrom":subQ0}),1.0]])]});}
            extrude(context, id + "F11", {"entities" : qUnion([Q0, Q1]), "depth" : 3.5 * mm, "offsetDistance" : 25 * mm});
        }
        {
            var Q0;
            Q0=makeQuery(id+"F0.imprint","IMPRINT",FACE,{"disambiguationData":[TD([[makeQuery(id+"F0.imprint","IMPRINT",EDGE,{"derivedFrom":sQuery(id+"F0.wireOp",EDGE,"E3")}),1.0]])]});
            var Q1;
            Q1=makeQuery(id+"F0.imprint","IMPRINT",FACE,{"disambiguationData":[TD([[makeQuery(id+"F0.imprint","IMPRINT",EDGE,{"derivedFrom":sQuery(id+"F0.wireOp",EDGE,"E6")}),1.0]])]});
            extrude(context, id + "F12", {"entities" : qUnion([Q0, Q1]), "operationType" : NewBodyOperationType.ADD, "depth" : 5 * mm, "offsetDistance" : 25 * mm});
        }
        {
            var Q0;
            {var subQ0=sQuery(id+"F1.wireOp",EDGE,"E60");Q0=makeQuery(id+"F1.imprint","IMPRINT",FACE,{"disambiguationData":[TD([[makeQuery(id+"F1.imprint","IMPRINT",EDGE,{"derivedFrom":subQ0}),1.0]])]});}
            var Q1;
            Q1=makeQuery(id+"F1.imprint","IMPRINT",FACE,{"disambiguationData":[TD([[makeQuery(id+"F1.imprint","IMPRINT",EDGE,{"derivedFrom":sQuery(id+"F1.wireOp",EDGE,"E62")}),-1.0]])]});
            extrude(context, id + "F13", {"entities" : qUnion([Q0, Q1]), "depth" : 3.5 * mm, "offsetDistance" : 25 * mm});
        }
        {
            var Q0;
            {var subQ0=sQuery(id+"F1.wireOp",EDGE,"E81");Q0=makeQuery(id+"F1.imprint","IMPRINT",FACE,{"disambiguationData":[TD([[makeQuery(id+"F1.imprint","IMPRINT",EDGE,{"derivedFrom":subQ0}),-1.0]])]});}
            extrude(context, id + "F14", {"entities" : qUnion([Q0]), "operationType" : NewBodyOperationType.ADD, "depth" : 4 * mm, "offsetDistance" : 25 * mm});
        }
        {
            var Q0;
            {var subQ1=sQuery(id+"F1.wireOp",EDGE,"E82");Q0=makeQuery(id+"F1.imprint","IMPRINT",FACE,{"disambiguationData":[TD([[makeQuery(id+"F1.imprint","IMPRINT",EDGE,{"derivedFrom":subQ1}),-1.0]])]});}
            extrude(context, id + "F15", {"entities" : qUnion([Q0]), "operationType" : NewBodyOperationType.ADD, "depth" : 5 * mm, "offsetDistance" : 25 * mm});
        }
        {
            var Q0;
            Q0=makeQuery(id+"F2.imprint","IMPRINT",FACE,{"disambiguationData":[TD([[makeQuery(id+"F2.imprint","IMPRINT",EDGE,{"derivedFrom":sQuery(id+"F2.wireOp",EDGE,"E109.bottom")}),-1.0]])]});
            var Q1;
            {var subQ0=sQuery(id+"F2.wireOp",EDGE,"E107");Q1=makeQuery(id+"F2.imprint","IMPRINT",FACE,{"disambiguationData":[TD([[makeQuery(id+"F2.imprint","IMPRINT",EDGE,{"derivedFrom":subQ0}),1.0]])]});}
            extrude(context, id + "F16", {"entities" : qUnion([Q0, Q1]), "depth" : 3.5 * mm, "offsetDistance" : 25 * mm});
        }
        {
            var Q0;
            Q0=makeQuery(id+"F2.imprint","IMPRINT",FACE,{"disambiguationData":[TD([[makeQuery(id+"F2.imprint","IMPRINT",EDGE,{"derivedFrom":sQuery(id+"F2.wireOp",EDGE,"E127")}),-1.0]])]});
            var Q1;
            Q1=makeQuery(id+"F2.imprint","IMPRINT",FACE,{"disambiguationData":[TD([[makeQuery(id+"F2.imprint","IMPRINT",EDGE,{"derivedFrom":sQuery(id+"F2.wireOp",EDGE,"E110")}),1.0]])]});
            var Q2;
            Q2=makeQuery(id+"F2.imprint","IMPRINT",FACE,{"disambiguationData":[TD([[makeQuery(id+"F2.imprint","IMPRINT",EDGE,{"derivedFrom":sQuery(id+"F2.wireOp",EDGE,"E159.MirrorCS")}),1.0]])]});
            extrude(context, id + "F17", {"entities" : qUnion([Q0, Q1, Q2]), "operationType" : NewBodyOperationType.ADD, "depth" : 5 * mm, "offsetDistance" : 25 * mm});
        }
        {
            var Q0;
            {var subQ1=sQuery(id+"F3.wireOp",EDGE,"E199");Q0=makeQuery(id+"F3.imprint","IMPRINT",FACE,{"disambiguationData":[TD([[makeQuery(id+"F3.imprint","IMPRINT",EDGE,{"derivedFrom":subQ1}),1.0]])]});}
            var Q1;
            {var subQ0=sQuery(id+"F3.wireOp",EDGE,"E200");Q1=makeQuery(id+"F3.imprint","IMPRINT",FACE,{"disambiguationData":[TD([[makeQuery(id+"F3.imprint","IMPRINT",EDGE,{"derivedFrom":subQ0}),1.0]])]});}
            extrude(context, id + "F18", {"entities" : qUnion([Q0, Q1]), "depth" : 3.5 * mm, "offsetDistance" : 25 * mm});
        }
        {
            var Q0;
            Q0=makeQuery(id+"F3.imprint","IMPRINT",FACE,{"disambiguationData":[TD([[makeQuery(id+"F3.imprint","IMPRINT",EDGE,{"derivedFrom":sQuery(id+"F3.wireOp",EDGE,"E216")}),-1.0]])]});
            var Q1;
            Q1=makeQuery(id+"F3.imprint","IMPRINT",FACE,{"disambiguationData":[TD([[makeQuery(id+"F3.imprint","IMPRINT",EDGE,{"derivedFrom":sQuery(id+"F3.wireOp",EDGE,"E206")}),1.0]])]});
            var Q2;
            Q2=makeQuery(id+"F3.imprint","IMPRINT",FACE,{"disambiguationData":[TD([[makeQuery(id+"F3.imprint","IMPRINT",EDGE,{"derivedFrom":sQuery(id+"F3.wireOp",EDGE,"E239.MirrorCS")}),1.0]])]});
            var Q3;
            Q3=makeQuery(id+"F3.imprint","IMPRINT",FACE,{"disambiguationData":[TD([[makeQuery(id+"F3.imprint","IMPRINT",EDGE,{"derivedFrom":sQuery(id+"F3.wireOp",EDGE,"E202")}),1.0]])]});
            extrude(context, id + "F19", {"entities" : qUnion([Q0, Q1, Q2, Q3]), "operationType" : NewBodyOperationType.ADD, "depth" : 5 * mm, "offsetDistance" : 25 * mm});
        }
        {
            var Q0;
            Q0=makeQuery(id+"F4.imprint","IMPRINT",FACE,{"disambiguationData":[TD([[makeQuery(id+"F4.imprint","IMPRINT",EDGE,{"derivedFrom":sQuery(id+"F4.wireOp",EDGE,"E247")}),1.0]])]});
            extrude(context, id + "F20", {"entities" : qUnion([Q0]), "depth" : 3.5 * mm, "offsetDistance" : 25 * mm});
        }
        {
            var Q0;
            Q0=makeQuery(id+"F4.imprint","IMPRINT",FACE,{"disambiguationData":[TD([[makeQuery(id+"F4.imprint","IMPRINT",EDGE,{"derivedFrom":sQuery(id+"F4.wireOp",EDGE,"E250")}),1.0]])]});
            extrude(context, id + "F21", {"entities" : qUnion([Q0]), "operationType" : NewBodyOperationType.ADD, "depth" : 5 * mm, "offsetDistance" : 25 * mm});
        }
        {
            var Q0;
            {var subQ0=sQuery(id+"F5.wireOp",EDGE,"E304");Q0=makeQuery(id+"F5.imprint","IMPRINT",FACE,{"disambiguationData":[TD([[makeQuery(id+"F5.imprint","IMPRINT",EDGE,{"derivedFrom":subQ0}),1.0]])]});}
            extrude(context, id + "F22", {"entities" : qUnion([Q0]), "depth" : 5 * mm, "offsetDistance" : 25 * mm});
        }
        {
            var Q0;
            {var subQ3=sQuery(id+"F5.wireOp",EDGE,"E333");Q0=makeQuery(id+"F5.imprint","IMPRINT",FACE,{"disambiguationData":[TD([[makeQuery(id+"F5.imprint","IMPRINT",EDGE,{"derivedFrom":subQ3}),1.0]])]});}
            extrude(context, id + "F23", {"entities" : qUnion([Q0]), "operationType" : NewBodyOperationType.ADD, "depth" : 3.5 * mm, "offsetDistance" : 25 * mm});
        }
        {
            var Q0;
            Q0=makeQuery(id+"F6.imprint","IMPRINT",FACE,{"disambiguationData":[TD([[makeQuery(id+"F6.imprint","IMPRINT",EDGE,{"derivedFrom":sQuery(id+"F6.wireOp",EDGE,"E364")}),-1.0]])]});
            extrude(context, id + "F24", {"entities" : qUnion([Q0]), "depth" : 3.5 * mm, "offsetDistance" : 25 * mm});
        }
        {
            var Q0;
            {var subQ6=sQuery(id+"F6.wireOp",EDGE,"E338");Q0=makeQuery(id+"F6.imprint","IMPRINT",FACE,{"disambiguationData":[TD([[makeQuery(id+"F6.imprint","IMPRINT",EDGE,{"derivedFrom":subQ6}),-1.0]])]});}
            extrude(context, id + "F25", {"entities" : qUnion([Q0]), "operationType" : NewBodyOperationType.ADD, "depth" : 5 * mm, "offsetDistance" : 25 * mm});
        }
        {
            var Q0;
            Q0=makeQuery(id+"F7.imprint","IMPRINT",FACE,{"disambiguationData":[TD([[makeQuery(id+"F7.imprint","IMPRINT",EDGE,{"derivedFrom":sQuery(id+"F7.wireOp",EDGE,"E370")}),-1.0]])]});
            extrude(context, id + "F26", {"entities" : qUnion([Q0]), "depth" : 5 * mm, "offsetDistance" : 25 * mm});
        }
        {
            var Q0;
            {var subQ0=sQuery(id+"F7.wireOp",EDGE,"E444");Q0=makeQuery(id+"F7.imprint","IMPRINT",FACE,{"disambiguationData":[TD([[makeQuery(id+"F7.imprint","IMPRINT",EDGE,{"derivedFrom":subQ0}),1.0]])]});}
            extrude(context, id + "F27", {"entities" : qUnion([Q0]), "operationType" : NewBodyOperationType.ADD, "depth" : 3.5 * mm, "offsetDistance" : 25 * mm});
        }
        {
            var Q0;
            Q0=makeQuery(id+"F8.imprint","IMPRINT",FACE,{"disambiguationData":[TD([[makeQuery(id+"F8.imprint","IMPRINT",EDGE,{"derivedFrom":sQuery(id+"F8.wireOp",EDGE,"E447")}),1.0]])]});
            extrude(context, id + "F28", {"entities" : qUnion([Q0]), "depth" : 5 * mm, "offsetDistance" : 25 * mm});
        }
        {
            var Q0;
            {var subQ0=sQuery(id+"F8.wireOp",EDGE,"E458");Q0=makeQuery(id+"F8.imprint","IMPRINT",FACE,{"disambiguationData":[TD([[makeQuery(id+"F8.imprint","IMPRINT",EDGE,{"derivedFrom":subQ0}),1.0]])]});}
            extrude(context, id + "F29", {"entities" : qUnion([Q0]), "operationType" : NewBodyOperationType.ADD, "depth" : 3.5 * mm, "offsetDistance" : 25 * mm});
        }
        {
            var Q0;
            {var subQ0=sQuery(id+"F9.wireOp",EDGE,"E487.trimOffspring");Q0=makeQuery(id+"F9.imprint","IMPRINT",FACE,{"disambiguationData":[TD([[makeQuery(id+"F9.imprint","IMPRINT",EDGE,{"derivedFrom":subQ0}),-1.0]])]});}
            extrude(context, id + "F30", {"entities" : qUnion([Q0]), "depth" : 3.5 * mm, "offsetDistance" : 25 * mm});
        }
        {
            var Q0;
            Q0=makeQuery(id+"F9.imprint","IMPRINT",FACE,{"disambiguationData":[TD([[makeQuery(id+"F9.imprint","IMPRINT",EDGE,{"derivedFrom":sQuery(id+"F9.wireOp",EDGE,"E461")}),-1.0]])]});
            extrude(context, id + "F31", {"entities" : qUnion([Q0]), "operationType" : NewBodyOperationType.ADD, "depth" : 5 * mm, "offsetDistance" : 25 * mm});
        }
        {
            var Q0;
            Q0=makeQuery(id+"F9.imprint","IMPRINT",FACE,{"disambiguationData":[TD([[makeQuery(id+"F9.imprint","IMPRINT",EDGE,{"derivedFrom":sQuery(id+"F9.wireOp",EDGE,"E462")}),-1.0]])]});
            extrude(context, id + "F32", {"entities" : qUnion([Q0]), "operationType" : NewBodyOperationType.ADD, "depth" : 4 * mm, "offsetDistance" : 25 * mm});
        }
        {
            var Q0;
            Q0=makeQuery(id+"F10.imprint","IMPRINT",FACE,{"disambiguationData":[TD([[makeQuery(id+"F10.imprint","IMPRINT",EDGE,{"derivedFrom":sQuery(id+"F10.wireOp",EDGE,"E567")}),-1.0]])]});
            extrude(context, id + "F33", {"entities" : qUnion([Q0]), "depth" : 3.5 * mm, "offsetDistance" : 25 * mm});
        }
        {
            var Q0;
            Q0=makeQuery(id+"F10.imprint","IMPRINT",FACE,{"disambiguationData":[TD([[makeQuery(id+"F10.imprint","IMPRINT",EDGE,{"derivedFrom":sQuery(id+"F10.wireOp",EDGE,"E495")}),1.0]])]});
            extrude(context, id + "F34", {"entities" : qUnion([Q0]), "operationType" : NewBodyOperationType.ADD, "depth" : 5 * mm, "offsetDistance" : 25 * mm});
        }
    });
